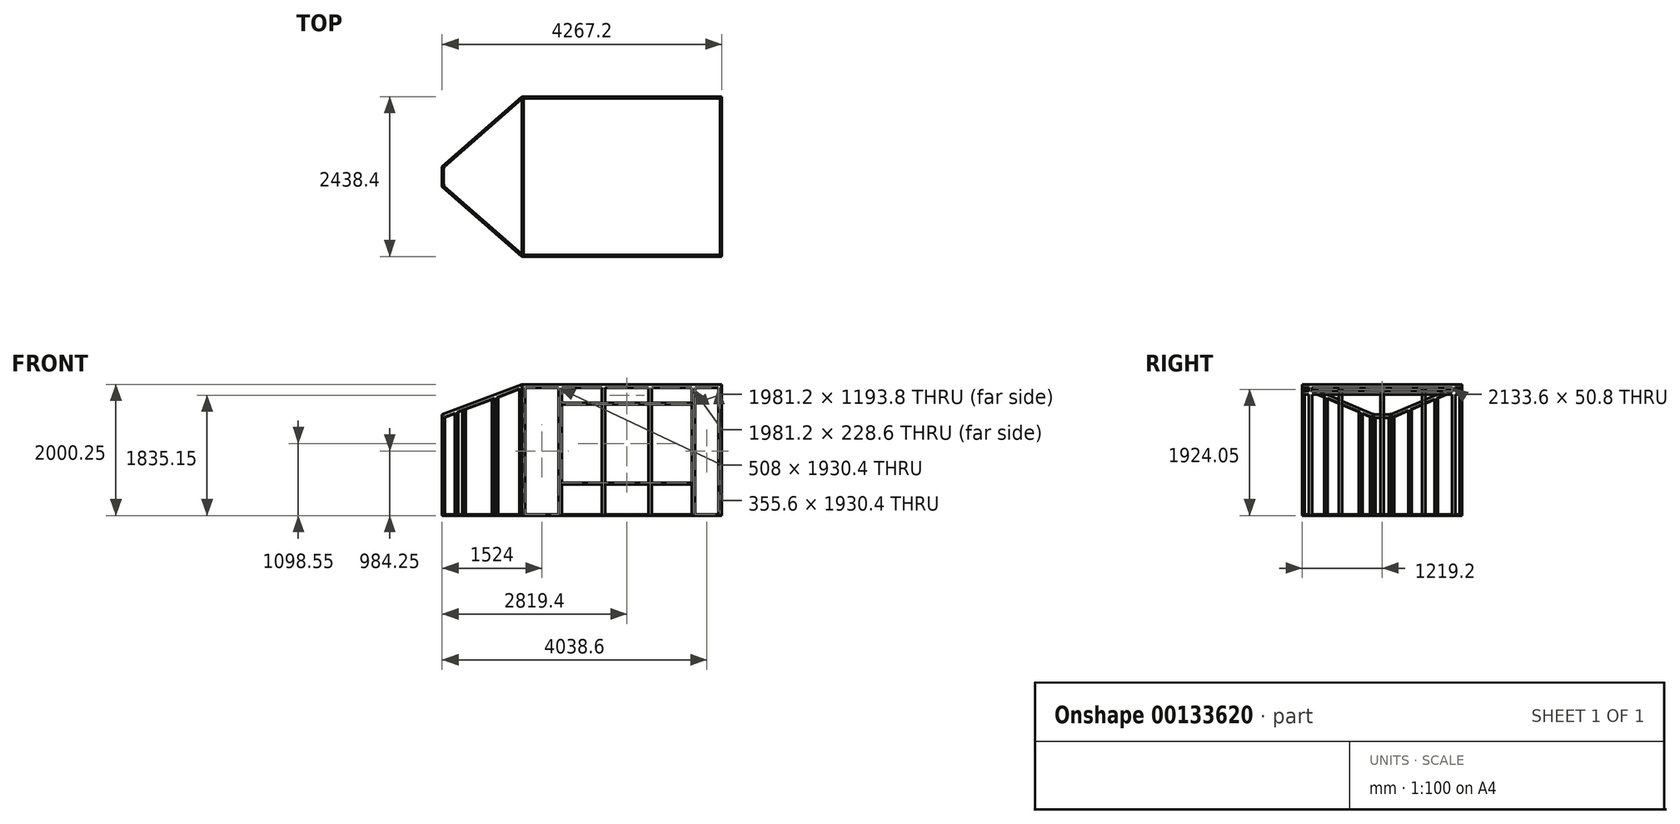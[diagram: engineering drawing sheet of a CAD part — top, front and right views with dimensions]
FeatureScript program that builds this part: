
annotation { "Feature Type Name" : "Feature", "Feature Type Description" : "" }
export const myFeature = defineFeature(function(context is Context, id is Id, definition is map)
    precondition{}
    {
        {
            var Q0;
            Q0=qCreatedBy(makeId("Top.planeOp"),FACE);
            var sketch = newSketch(context, id + "F0", { "sketchPlane" : qUnion([Q0])});
            skLineSegment(sketch, "E0.bottom", {"start": v(0, 0) * mm, "end": v(3048, 0) * mm});
            skLineSegment(sketch, "E0.top", {"start": v(0, 2438.4) * mm, "end": v(3048, 2438.4) * mm});
            skLineSegment(sketch, "E0.left", {"start": v(0, 0) * mm, "end": v(0, 2438.4) * mm});
            skLineSegment(sketch, "E0.right", {"start": v(3048, 0) * mm, "end": v(3048, 2438.4) * mm});
            skLineSegment(sketch, "E1", {"start": v(0, 1219.2) * mm, "end": v(-1219.2, 1219.2) * mm});
            skPoint(sketch, "E1.endSnap0", {"position": v(0, 1219.2) * mm});
            skLineSegment(sketch, "E2", {"start": v(-1219.2, 1219.2) * mm, "end": v(-1219.2, 1371.6) * mm});
            skLineSegment(sketch, "E3", {"start": v(-1219.2, 1371.6) * mm, "end": v(0, 2438.4) * mm});
            skLineSegment(sketch, "E4", {"start": v(-1219.2, 1219.2) * mm, "end": v(-1219.2, 1066.8) * mm});
            skLineSegment(sketch, "E5", {"start": v(-1219.2, 1066.8) * mm, "end": v(0, 0) * mm});
            skSolve(sketch);
        }
        {
            var Q0;
            {var subQ2=sQuery(id+"F0.wireOp",EDGE,"E1");Q0=makeQuery(id+"F0.imprint","IMPRINT",FACE,{"disambiguationData":[TD([[makeQuery(id+"F0.imprint","IMPRINT",EDGE,{"derivedFrom":subQ2}),-1.0]])]});}
            var Q1;
            {var subQ3=sQuery(id+"F0.wireOp",EDGE,"E0.bottom");Q1=makeQuery(id+"F0.imprint","IMPRINT",FACE,{"disambiguationData":[TD([[makeQuery(id+"F0.imprint","IMPRINT",EDGE,{"derivedFrom":subQ3}),1.0]])]});}
            var Q2;
            {var subQ2=sQuery(id+"F0.wireOp",EDGE,"E1");Q2=makeQuery(id+"F0.imprint","IMPRINT",FACE,{"disambiguationData":[TD([[makeQuery(id+"F0.imprint","IMPRINT",EDGE,{"derivedFrom":subQ2}),1.0]])]});}
            extrude(context, id + "F1", {"entities" : qUnion([Q0, Q1, Q2]), "depth" : 19.05 * mm});
        }
        {
            var Q0;
            Q0=makeQuery(id+"F1.opExtrude","CAP_FACE",FACE,{"disambiguationData":[OSD([sQuery(id+"F0.wireOp",EDGE,"E0.bottom"),sQuery(id+"F0.wireOp",EDGE,"E0.top"),sQuery(id+"F0.wireOp",EDGE,"E0.right"),sQuery(id+"F0.wireOp",EDGE,"E2"),sQuery(id+"F0.wireOp",EDGE,"E3"),sQuery(id+"F0.wireOp",EDGE,"E4"),sQuery(id+"F0.wireOp",EDGE,"E5")])],"isStart":false});
            var sketch = newSketch(context, id + "F2", { "sketchPlane" : qUnion([Q0])});
            skLineSegment(sketch, "E6.bottom", {"start": v(0, 2438.4) * mm, "end": v(50.8, 2438.4) * mm});
            skLineSegment(sketch, "E6.top", {"start": v(0, 2413) * mm, "end": v(50.8, 2413) * mm});
            skLineSegment(sketch, "E6.left", {"start": v(0, 2438.4) * mm, "end": v(0, 2413) * mm});
            skLineSegment(sketch, "E6.right", {"start": v(50.8, 2438.4) * mm, "end": v(50.8, 2413) * mm});
            skLineSegment(sketch, "E7.bottom", {"start": v(3048, 2438.4) * mm, "end": v(2997.2, 2438.4) * mm});
            skLineSegment(sketch, "E7.top", {"start": v(3048, 2413) * mm, "end": v(2997.2, 2413) * mm});
            skLineSegment(sketch, "E7.left", {"start": v(3048, 2438.4) * mm, "end": v(3048, 2413) * mm});
            skLineSegment(sketch, "E7.right", {"start": v(2997.2, 2438.4) * mm, "end": v(2997.2, 2413) * mm});
            skLineSegment(sketch, "E8.bottom", {"start": v(3048, 0) * mm, "end": v(2997.2, 0) * mm});
            skLineSegment(sketch, "E8.top", {"start": v(3048, 25.4) * mm, "end": v(2997.2, 25.4) * mm});
            skLineSegment(sketch, "E8.left", {"start": v(3048, 0) * mm, "end": v(3048, 25.4) * mm});
            skLineSegment(sketch, "E8.right", {"start": v(2997.2, 0) * mm, "end": v(2997.2, 25.4) * mm});
            skLineSegment(sketch, "E9.bottom", {"start": v(0, 0) * mm, "end": v(50.8, 0) * mm});
            skLineSegment(sketch, "E9.top", {"start": v(0, 25.4) * mm, "end": v(50.8, 25.4) * mm});
            skLineSegment(sketch, "E9.left", {"start": v(0, 0) * mm, "end": v(0, 25.4) * mm});
            skLineSegment(sketch, "E9.right", {"start": v(50.8, 0) * mm, "end": v(50.8, 25.4) * mm});
            skLineSegment(sketch, "E10.bottom", {"start": v(558.8, 2438.4) * mm, "end": v(609.6, 2438.4) * mm});
            skLineSegment(sketch, "E10.top", {"start": v(558.8, 2413) * mm, "end": v(609.6, 2413) * mm});
            skLineSegment(sketch, "E10.left", {"start": v(558.8, 2438.4) * mm, "end": v(558.8, 2413) * mm});
            skLineSegment(sketch, "E10.right", {"start": v(609.6, 2438.4) * mm, "end": v(609.6, 2413) * mm});
            skLineSegment(sketch, "E11.bottom", {"start": v(2641.6, 2438.4) * mm, "end": v(2590.8, 2438.4) * mm});
            skLineSegment(sketch, "E11.top", {"start": v(2641.6, 2413) * mm, "end": v(2590.8, 2413) * mm});
            skLineSegment(sketch, "E11.left", {"start": v(2641.6, 2438.4) * mm, "end": v(2641.6, 2413) * mm});
            skLineSegment(sketch, "E11.right", {"start": v(2590.8, 2438.4) * mm, "end": v(2590.8, 2413) * mm});
            skLineSegment(sketch, "E12.bottom", {"start": v(558.8, 0) * mm, "end": v(609.6, 0) * mm});
            skLineSegment(sketch, "E12.top", {"start": v(558.8, 25.4) * mm, "end": v(609.6, 25.4) * mm});
            skLineSegment(sketch, "E12.left", {"start": v(558.8, 0) * mm, "end": v(558.8, 25.4) * mm});
            skLineSegment(sketch, "E12.right", {"start": v(609.6, 0) * mm, "end": v(609.6, 25.4) * mm});
            skLineSegment(sketch, "E13.bottom", {"start": v(2641.6, 0) * mm, "end": v(2590.8, 0) * mm});
            skLineSegment(sketch, "E13.top", {"start": v(2641.6, 25.4) * mm, "end": v(2590.8, 25.4) * mm});
            skLineSegment(sketch, "E13.left", {"start": v(2641.6, 0) * mm, "end": v(2641.6, 25.4) * mm});
            skLineSegment(sketch, "E13.right", {"start": v(2590.8, 0) * mm, "end": v(2590.8, 25.4) * mm});
            skLineSegment(sketch, "E14.bottom", {"start": v(1981.2, 0) * mm, "end": v(1930.4, 0) * mm});
            skLineSegment(sketch, "E14.top", {"start": v(1981.2, 25.4) * mm, "end": v(1930.4, 25.4) * mm});
            skLineSegment(sketch, "E14.left", {"start": v(1981.2, 0) * mm, "end": v(1981.2, 25.4) * mm});
            skLineSegment(sketch, "E14.right", {"start": v(1930.4, 0) * mm, "end": v(1930.4, 25.4) * mm});
            skLineSegment(sketch, "E15.bottom", {"start": v(1270, 0) * mm, "end": v(1219.2, 0) * mm});
            skLineSegment(sketch, "E15.top", {"start": v(1270, 25.4) * mm, "end": v(1219.2, 25.4) * mm});
            skLineSegment(sketch, "E15.left", {"start": v(1270, 0) * mm, "end": v(1270, 25.4) * mm});
            skLineSegment(sketch, "E15.right", {"start": v(1219.2, 0) * mm, "end": v(1219.2, 25.4) * mm});
            skLineSegment(sketch, "E16.bottom", {"start": v(0, 1879.6) * mm, "end": v(25.4, 1879.6) * mm});
            skLineSegment(sketch, "E16.top", {"start": v(0, 1828.8) * mm, "end": v(25.4, 1828.8) * mm});
            skLineSegment(sketch, "E16.left", {"start": v(0, 1879.6) * mm, "end": v(0, 1828.8) * mm});
            skLineSegment(sketch, "E16.right", {"start": v(25.4, 1879.6) * mm, "end": v(25.4, 1828.8) * mm});
            skLineSegment(sketch, "E17.bottom", {"start": v(0, 558.8) * mm, "end": v(25.4, 558.8) * mm});
            skLineSegment(sketch, "E17.top", {"start": v(0, 609.6) * mm, "end": v(25.4, 609.6) * mm});
            skLineSegment(sketch, "E17.left", {"start": v(0, 558.8) * mm, "end": v(0, 609.6) * mm});
            skLineSegment(sketch, "E18", {"start": v(25.4, 609.6) * mm, "end": v(25.4, 558.8) * mm});
            skLineSegment(sketch, "E19", {"start": v(0, 1193.8) * mm, "end": v(0, 1244.6) * mm});
            skPoint(sketch, "E20.endSnap0", {"position": v(0, 1219.2) * mm});
            skLineSegment(sketch, "E21", {"start": v(25.4, 1219.2) * mm, "end": v(25.4, 1244.6) * mm});
            skLineSegment(sketch, "E22", {"start": v(25.4, 1244.6) * mm, "end": v(0, 1244.6) * mm});
            skLineSegment(sketch, "E23.MirrorCS", {"start": v(25.4, 1193.8) * mm, "end": v(0, 1193.8) * mm});
            skLineSegment(sketch, "E24.MirrorCS", {"start": v(25.4, 1219.2) * mm, "end": v(25.4, 1193.8) * mm});
            skSolve(sketch);
        }
        {
            var Q0;
            Q0=makeQuery(id+"F2.imprint","IMPRINT",FACE,{"disambiguationData":[TD([[makeQuery(id+"F2.imprint","IMPRINT",EDGE,{"derivedFrom":sQuery(id+"F2.wireOp",EDGE,"E6.bottom")}),-1.0]])]});
            var Q1;
            Q1=makeQuery(id+"F2.imprint","IMPRINT",FACE,{"disambiguationData":[TD([[makeQuery(id+"F2.imprint","IMPRINT",EDGE,{"derivedFrom":sQuery(id+"F2.wireOp",EDGE,"E10.bottom")}),-1.0]])]});
            var Q2;
            Q2=makeQuery(id+"F2.imprint","IMPRINT",FACE,{"disambiguationData":[TD([[makeQuery(id+"F2.imprint","IMPRINT",EDGE,{"derivedFrom":sQuery(id+"F2.wireOp",EDGE,"E11.bottom")}),-1.0]])]});
            var Q3;
            Q3=makeQuery(id+"F2.imprint","IMPRINT",FACE,{"disambiguationData":[TD([[makeQuery(id+"F2.imprint","IMPRINT",EDGE,{"derivedFrom":sQuery(id+"F2.wireOp",EDGE,"E7.bottom")}),-1.0]])]});
            var Q4;
            Q4=makeQuery(id+"F2.imprint","IMPRINT",FACE,{"disambiguationData":[TD([[makeQuery(id+"F2.imprint","IMPRINT",EDGE,{"derivedFrom":sQuery(id+"F2.wireOp",EDGE,"E8.bottom")}),1.0]])]});
            var Q5;
            Q5=makeQuery(id+"F2.imprint","IMPRINT",FACE,{"disambiguationData":[TD([[makeQuery(id+"F2.imprint","IMPRINT",EDGE,{"derivedFrom":sQuery(id+"F2.wireOp",EDGE,"E13.bottom")}),1.0]])]});
            var Q6;
            Q6=makeQuery(id+"F2.imprint","IMPRINT",FACE,{"disambiguationData":[TD([[makeQuery(id+"F2.imprint","IMPRINT",EDGE,{"derivedFrom":sQuery(id+"F2.wireOp",EDGE,"E14.bottom")}),1.0]])]});
            var Q7;
            Q7=makeQuery(id+"F2.imprint","IMPRINT",FACE,{"disambiguationData":[TD([[makeQuery(id+"F2.imprint","IMPRINT",EDGE,{"derivedFrom":sQuery(id+"F2.wireOp",EDGE,"E15.bottom")}),1.0]])]});
            var Q8;
            Q8=makeQuery(id+"F2.imprint","IMPRINT",FACE,{"disambiguationData":[TD([[makeQuery(id+"F2.imprint","IMPRINT",EDGE,{"derivedFrom":sQuery(id+"F2.wireOp",EDGE,"E12.bottom")}),1.0]])]});
            var Q9;
            Q9=makeQuery(id+"F2.imprint","IMPRINT",FACE,{"disambiguationData":[TD([[makeQuery(id+"F2.imprint","IMPRINT",EDGE,{"derivedFrom":sQuery(id+"F2.wireOp",EDGE,"E9.bottom")}),1.0]])]});
            var Q10;
            Q10=makeQuery(id+"F2.imprint","IMPRINT",FACE,{"disambiguationData":[TD([[makeQuery(id+"F2.imprint","IMPRINT",EDGE,{"derivedFrom":sQuery(id+"F2.wireOp",EDGE,"E17.bottom")}),1.0]])]});
            var Q11;
            Q11=makeQuery(id+"F2.imprint","IMPRINT",FACE,{"disambiguationData":[TD([[makeQuery(id+"F2.imprint","IMPRINT",EDGE,{"derivedFrom":sQuery(id+"F2.wireOp",EDGE,"E19")}),-1.0]])]});
            var Q12;
            Q12=makeQuery(id+"F2.imprint","IMPRINT",FACE,{"disambiguationData":[TD([[makeQuery(id+"F2.imprint","IMPRINT",EDGE,{"derivedFrom":sQuery(id+"F2.wireOp",EDGE,"E16.bottom")}),-1.0]])]});
            extrude(context, id + "F3", {"entities" : qUnion([Q0, Q1, Q2, Q3, Q4, Q5, Q6, Q7, Q8, Q9, Q10, Q11, Q12]), "operationType" : NewBodyOperationType.ADD, "depth" : 1981.2 * mm});
        }
        {
            var Q0;
            Q0=makeQuery(id+"F1.opExtrude","CAP_FACE",FACE,{"disambiguationData":[OSD([sQuery(id+"F0.wireOp",EDGE,"E0.bottom"),sQuery(id+"F0.wireOp",EDGE,"E0.top"),sQuery(id+"F0.wireOp",EDGE,"E0.right"),sQuery(id+"F0.wireOp",EDGE,"E2"),sQuery(id+"F0.wireOp",EDGE,"E3"),sQuery(id+"F0.wireOp",EDGE,"E4"),sQuery(id+"F0.wireOp",EDGE,"E5")])],"isStart":false});
            var sketch = newSketch(context, id + "F4", { "sketchPlane" : qUnion([Q0])});
            skLineSegment(sketch, "E25.bottom", {"start": v(1981.2, 2438.4) * mm, "end": v(1930.4, 2438.4) * mm});
            skLineSegment(sketch, "E25.top", {"start": v(1981.2, 2413) * mm, "end": v(1930.4, 2413) * mm});
            skLineSegment(sketch, "E25.left", {"start": v(1981.2, 2438.4) * mm, "end": v(1981.2, 2413) * mm});
            skLineSegment(sketch, "E25.right", {"start": v(1930.4, 2438.4) * mm, "end": v(1930.4, 2413) * mm});
            skLineSegment(sketch, "E26.bottom", {"start": v(1270, 2438.4) * mm, "end": v(1219.2, 2438.4) * mm});
            skLineSegment(sketch, "E26.top", {"start": v(1270, 2413) * mm, "end": v(1219.2, 2413) * mm});
            skLineSegment(sketch, "E26.left", {"start": v(1270, 2438.4) * mm, "end": v(1270, 2413) * mm});
            skLineSegment(sketch, "E26.right", {"start": v(1219.2, 2438.4) * mm, "end": v(1219.2, 2413) * mm});
            skPoint(sketch, "E27", {"position": v(609.6, 0) * mm});
            skPoint(sketch, "E28", {"position": v(1270, 0) * mm});
            skSolve(sketch);
        }
        {
            var Q0;
            Q0=makeQuery(id+"F4.imprint","IMPRINT",FACE,{"disambiguationData":[TD([[makeQuery(id+"F4.imprint","IMPRINT",EDGE,{"derivedFrom":sQuery(id+"F4.wireOp",EDGE,"E25.bottom")}),-1.0]])]});
            var Q1;
            Q1=makeQuery(id+"F4.imprint","IMPRINT",FACE,{"disambiguationData":[TD([[makeQuery(id+"F4.imprint","IMPRINT",EDGE,{"derivedFrom":sQuery(id+"F4.wireOp",EDGE,"E26.bottom")}),-1.0]])]});
            extrude(context, id + "F5", {"entities" : qUnion([Q0, Q1]), "operationType" : NewBodyOperationType.ADD, "depth" : 457.2 * mm});
        }
        {
            var Q0;
            Q0=makeQuery(id+"F3.opExtrude","SWEPT_FACE",FACE,{"disambiguationData":[OSD([sQuery(id+"F2.wireOp",EDGE,"E10.right")])]});
            var sketch = newSketch(context, id + "F6", { "sketchPlane" : qUnion([Q0])});
            skLineSegment(sketch, "E29.bottom", {"start": v(2438.4, 476.25) * mm, "end": v(2413, 476.25) * mm});
            skLineSegment(sketch, "E29.top", {"start": v(2438.4, 501.65) * mm, "end": v(2413, 501.65) * mm});
            skLineSegment(sketch, "E29.left", {"start": v(2438.4, 476.25) * mm, "end": v(2438.4, 501.65) * mm});
            skLineSegment(sketch, "E29.right", {"start": v(2413, 476.25) * mm, "end": v(2413, 501.65) * mm});
            skLineSegment(sketch, "E30.bottom", {"start": v(2438.4, 1695.45) * mm, "end": v(2413, 1695.45) * mm});
            skLineSegment(sketch, "E30.top", {"start": v(2438.4, 1720.85) * mm, "end": v(2413, 1720.85) * mm});
            skLineSegment(sketch, "E30.left", {"start": v(2438.4, 1695.45) * mm, "end": v(2438.4, 1720.85) * mm});
            skLineSegment(sketch, "E30.right", {"start": v(2413, 1695.45) * mm, "end": v(2413, 1720.85) * mm});
            skSolve(sketch);
        }
        {
            var Q0;
            Q0=makeQuery(id+"F6.imprint","IMPRINT",FACE,{"disambiguationData":[TD([[makeQuery(id+"F6.imprint","IMPRINT",EDGE,{"derivedFrom":sQuery(id+"F6.wireOp",EDGE,"E30.bottom")}),-1.0]])]});
            var Q1;
            Q1=makeQuery(id+"F6.imprint","IMPRINT",FACE,{"disambiguationData":[TD([[makeQuery(id+"F6.imprint","IMPRINT",EDGE,{"derivedFrom":sQuery(id+"F6.wireOp",EDGE,"E29.bottom")}),-1.0]])]});
            var Q2;
            Q2=makeQuery(id+"F3.opExtrude","SWEPT_FACE",FACE,{"disambiguationData":[OSD([sQuery(id+"F2.wireOp",EDGE,"E11.right")])]});
            extrude(context, id + "F7", {"entities" : qUnion([Q0, Q1]), "operationType" : NewBodyOperationType.ADD, "endBound" : BoundingType.UP_TO_SURFACE, "endBoundEntityFace" : qUnion([Q2]), "depth" : 25.4 * mm});
        }
        {
            var Q0;
            Q0=makeQuery(id+"F1.opExtrude","CAP_FACE",FACE,{"disambiguationData":[OSD([sQuery(id+"F0.wireOp",EDGE,"E0.bottom"),sQuery(id+"F0.wireOp",EDGE,"E0.top"),sQuery(id+"F0.wireOp",EDGE,"E0.right"),sQuery(id+"F0.wireOp",EDGE,"E2"),sQuery(id+"F0.wireOp",EDGE,"E3"),sQuery(id+"F0.wireOp",EDGE,"E4"),sQuery(id+"F0.wireOp",EDGE,"E5")])],"isStart":false});
            var sketch = newSketch(context, id + "F8", { "sketchPlane" : qUnion([Q0])});
            skLineSegment(sketch, "E31.bottom", {"start": v(3048, 101.6) * mm, "end": v(3022.6, 101.6) * mm});
            skLineSegment(sketch, "E31.top", {"start": v(3048, 152.4) * mm, "end": v(3022.6, 152.4) * mm});
            skLineSegment(sketch, "E31.left", {"start": v(3048, 101.6) * mm, "end": v(3048, 152.4) * mm});
            skLineSegment(sketch, "E31.right", {"start": v(3022.6, 101.6) * mm, "end": v(3022.6, 152.4) * mm});
            skLineSegment(sketch, "E32.bottom", {"start": v(3048, 2336.8) * mm, "end": v(3022.6, 2336.8) * mm});
            skLineSegment(sketch, "E32.top", {"start": v(3048, 2286) * mm, "end": v(3022.6, 2286) * mm});
            skLineSegment(sketch, "E32.left", {"start": v(3048, 2336.8) * mm, "end": v(3048, 2286) * mm});
            skLineSegment(sketch, "E32.right", {"start": v(3022.6, 2336.8) * mm, "end": v(3022.6, 2286) * mm});
            skSolve(sketch);
        }
        {
            var Q0;
            Q0=makeQuery(id+"F8.imprint","IMPRINT",FACE,{"disambiguationData":[TD([[makeQuery(id+"F8.imprint","IMPRINT",EDGE,{"derivedFrom":sQuery(id+"F8.wireOp",EDGE,"E32.bottom")}),1.0]])]});
            var Q1;
            Q1=makeQuery(id+"F8.imprint","IMPRINT",FACE,{"disambiguationData":[TD([[makeQuery(id+"F8.imprint","IMPRINT",EDGE,{"derivedFrom":sQuery(id+"F8.wireOp",EDGE,"E31.bottom")}),-1.0]])]});
            extrude(context, id + "F9", {"entities" : qUnion([Q0, Q1]), "operationType" : NewBodyOperationType.ADD, "depth" : 1981.2 * mm});
        }
        {
            var Q0;
            Q0=makeQuery(id+"F9.boolean.opBoolean","MERGE",FACE,{"derivedFrom":[makeQuery(id+"F3.boolean.opBoolean","MERGE",FACE,{"derivedFrom":[makeQuery(id+"F1.opExtrude","SWEPT_FACE",FACE,{"disambiguationData":[OSD([sQuery(id+"F0.wireOp",EDGE,"E0.right")])]}),makeQuery(id+"F3.opExtrude","SWEPT_FACE",FACE,{"disambiguationData":[OSD([sQuery(id+"F2.wireOp",EDGE,"E7.left")])]}),makeQuery(id+"F3.opExtrude","SWEPT_FACE",FACE,{"disambiguationData":[OSD([sQuery(id+"F2.wireOp",EDGE,"E8.left")])]})]}),makeQuery(id+"F9.opExtrude","SWEPT_FACE",FACE,{"disambiguationData":[OSD([sQuery(id+"F8.wireOp",EDGE,"E31.left")])]}),makeQuery(id+"F9.opExtrude","SWEPT_FACE",FACE,{"disambiguationData":[OSD([sQuery(id+"F8.wireOp",EDGE,"E32.left")])]})]});
            var sketch = newSketch(context, id + "F10", { "sketchPlane" : qUnion([Q0])});
            skLineSegment(sketch, "E33.bottom", {"start": v(2413, 2000.25) * mm, "end": v(2438.4, 2000.25) * mm});
            skLineSegment(sketch, "E33.top", {"start": v(2413, 1949.45) * mm, "end": v(2438.4, 1949.45) * mm});
            skLineSegment(sketch, "E33.left", {"start": v(2413, 2000.25) * mm, "end": v(2413, 1949.45) * mm});
            skLineSegment(sketch, "E33.right", {"start": v(2438.4, 2000.25) * mm, "end": v(2438.4, 1949.45) * mm});
            skSolve(sketch);
        }
        {
            var Q0;
            Q0=makeQuery(id+"F10.imprint","IMPRINT",FACE,{"disambiguationData":[TD([[makeQuery(id+"F10.imprint","IMPRINT",EDGE,{"derivedFrom":sQuery(id+"F10.wireOp",EDGE,"E33.bottom")}),-1.0]])]});
            var Q1;
            Q1=makeQuery(id+"F3.opExtrude","SWEPT_FACE",FACE,{"disambiguationData":[OSD([sQuery(id+"F2.wireOp",EDGE,"E6.right")])]});
            extrude(context, id + "F11", {"entities" : qUnion([Q0]), "operationType" : NewBodyOperationType.ADD, "endBound" : BoundingType.UP_TO_SURFACE, "oppositeDirection" : true, "endBoundEntityFace" : qUnion([Q1]), "depth" : 25.4 * mm});
        }
        {
            var Q0;
            Q0=makeQuery(id+"F9.boolean.opBoolean","MERGE",FACE,{"derivedFrom":[makeQuery(id+"F3.boolean.opBoolean","MERGE",FACE,{"derivedFrom":[makeQuery(id+"F1.opExtrude","SWEPT_FACE",FACE,{"disambiguationData":[OSD([sQuery(id+"F0.wireOp",EDGE,"E0.right")])]}),makeQuery(id+"F3.opExtrude","SWEPT_FACE",FACE,{"disambiguationData":[OSD([sQuery(id+"F2.wireOp",EDGE,"E7.left")])]}),makeQuery(id+"F3.opExtrude","SWEPT_FACE",FACE,{"disambiguationData":[OSD([sQuery(id+"F2.wireOp",EDGE,"E8.left")])]})]}),makeQuery(id+"F9.opExtrude","SWEPT_FACE",FACE,{"disambiguationData":[OSD([sQuery(id+"F8.wireOp",EDGE,"E31.left")])]}),makeQuery(id+"F9.opExtrude","SWEPT_FACE",FACE,{"disambiguationData":[OSD([sQuery(id+"F8.wireOp",EDGE,"E32.left")])]})]});
            var sketch = newSketch(context, id + "F12", { "sketchPlane" : qUnion([Q0])});
            skLineSegment(sketch, "E34.bottom", {"start": v(0, 2000.25) * mm, "end": v(25.4, 2000.25) * mm});
            skLineSegment(sketch, "E34.top", {"start": v(0, 1949.45) * mm, "end": v(25.4, 1949.45) * mm});
            skLineSegment(sketch, "E34.left", {"start": v(0, 2000.25) * mm, "end": v(0, 1949.45) * mm});
            skLineSegment(sketch, "E34.right", {"start": v(25.4, 2000.25) * mm, "end": v(25.4, 1949.45) * mm});
            skSolve(sketch);
        }
        {
            var Q0;
            Q0=makeQuery(id+"F12.imprint","IMPRINT",FACE,{"disambiguationData":[TD([[makeQuery(id+"F12.imprint","IMPRINT",EDGE,{"derivedFrom":sQuery(id+"F12.wireOp",EDGE,"E34.bottom")}),-1.0]])]});
            var Q1;
            Q1=makeQuery(id+"F3.opExtrude","SWEPT_FACE",FACE,{"disambiguationData":[OSD([sQuery(id+"F2.wireOp",EDGE,"E9.right")])]});
            extrude(context, id + "F13", {"entities" : qUnion([Q0]), "operationType" : NewBodyOperationType.ADD, "endBound" : BoundingType.UP_TO_SURFACE, "oppositeDirection" : true, "endBoundEntityFace" : qUnion([Q1]), "depth" : 25.4 * mm});
        }
        {
            var Q0;
            Q0=makeQuery(id+"F13.boolean.opBoolean","MERGE",FACE,{"derivedFrom":[makeQuery(id+"F3.boolean.opBoolean","MERGE",FACE,{"derivedFrom":[makeQuery(id+"F1.opExtrude","SWEPT_FACE",FACE,{"disambiguationData":[OSD([sQuery(id+"F0.wireOp",EDGE,"E0.bottom")])]}),makeQuery(id+"F3.opExtrude","SWEPT_FACE",FACE,{"disambiguationData":[OSD([sQuery(id+"F2.wireOp",EDGE,"E8.bottom")])]}),makeQuery(id+"F3.opExtrude","SWEPT_FACE",FACE,{"disambiguationData":[OSD([sQuery(id+"F2.wireOp",EDGE,"E9.bottom")])]}),makeQuery(id+"F3.opExtrude","SWEPT_FACE",FACE,{"disambiguationData":[OSD([sQuery(id+"F2.wireOp",EDGE,"E12.bottom")])]}),makeQuery(id+"F3.opExtrude","SWEPT_FACE",FACE,{"disambiguationData":[OSD([sQuery(id+"F2.wireOp",EDGE,"E13.bottom")])]}),makeQuery(id+"F3.opExtrude","SWEPT_FACE",FACE,{"disambiguationData":[OSD([sQuery(id+"F2.wireOp",EDGE,"E14.bottom")])]}),makeQuery(id+"F3.opExtrude","SWEPT_FACE",FACE,{"disambiguationData":[OSD([sQuery(id+"F2.wireOp",EDGE,"E15.bottom")])]})]}),makeQuery(id+"F13.opExtrude","SWEPT_FACE",FACE,{"disambiguationData":[OSD([sQuery(id+"F12.wireOp",EDGE,"E34.left")])]})]});
            var sketch = newSketch(context, id + "F14", { "sketchPlane" : qUnion([Q0])});
            skLineSegment(sketch, "E35.bottom", {"start": v(0, 2000.25) * mm, "end": v(25.4, 2000.25) * mm});
            skLineSegment(sketch, "E35.top", {"start": v(0, 1949.45) * mm, "end": v(25.4, 1949.45) * mm});
            skLineSegment(sketch, "E35.left", {"start": v(0, 2000.25) * mm, "end": v(0, 1949.45) * mm});
            skLineSegment(sketch, "E35.right", {"start": v(25.4, 2000.25) * mm, "end": v(25.4, 1949.45) * mm});
            skLineSegment(sketch, "E36.bottom", {"start": v(3048, 2000.25) * mm, "end": v(3022.6, 2000.25) * mm});
            skLineSegment(sketch, "E36.top", {"start": v(3048, 1949.45) * mm, "end": v(3022.6, 1949.45) * mm});
            skLineSegment(sketch, "E36.left", {"start": v(3048, 2000.25) * mm, "end": v(3048, 1949.45) * mm});
            skLineSegment(sketch, "E36.right", {"start": v(3022.6, 2000.25) * mm, "end": v(3022.6, 1949.45) * mm});
            skSolve(sketch);
        }
        {
            var Q0;
            Q0=makeQuery(id+"F14.imprint","IMPRINT",FACE,{"disambiguationData":[TD([[makeQuery(id+"F14.imprint","IMPRINT",EDGE,{"derivedFrom":sQuery(id+"F14.wireOp",EDGE,"E36.bottom")}),-1.0]])]});
            var Q1;
            Q1=makeQuery(id+"F14.imprint","IMPRINT",FACE,{"disambiguationData":[TD([[makeQuery(id+"F14.imprint","IMPRINT",EDGE,{"derivedFrom":sQuery(id+"F14.wireOp",EDGE,"E35.bottom")}),-1.0]])]});
            var Q2;
            Q2=makeQuery(id+"F11.boolean.opBoolean","MERGE",FACE,{"derivedFrom":[makeQuery(id+"F3.opExtrude","SWEPT_FACE",FACE,{"disambiguationData":[OSD([sQuery(id+"F2.wireOp",EDGE,"E6.top")])]}),makeQuery(id+"F3.opExtrude","SWEPT_FACE",FACE,{"disambiguationData":[OSD([sQuery(id+"F2.wireOp",EDGE,"E7.top")])]}),makeQuery(id+"F7.boolean.opBoolean","MERGE",FACE,{"derivedFrom":[makeQuery(id+"F3.opExtrude","SWEPT_FACE",FACE,{"disambiguationData":[OSD([sQuery(id+"F2.wireOp",EDGE,"E10.top")])]}),makeQuery(id+"F3.opExtrude","SWEPT_FACE",FACE,{"disambiguationData":[OSD([sQuery(id+"F2.wireOp",EDGE,"E11.top")])]}),makeQuery(id+"F5.opExtrude","SWEPT_FACE",FACE,{"disambiguationData":[OSD([sQuery(id+"F4.wireOp",EDGE,"E25.top")])]}),makeQuery(id+"F5.opExtrude","SWEPT_FACE",FACE,{"disambiguationData":[OSD([sQuery(id+"F4.wireOp",EDGE,"E26.top")])]}),makeQuery(id+"F7.opExtrude","SWEPT_FACE",FACE,{"disambiguationData":[OSD([sQuery(id+"F6.wireOp",EDGE,"E29.right")])]}),makeQuery(id+"F7.opExtrude","SWEPT_FACE",FACE,{"disambiguationData":[OSD([sQuery(id+"F6.wireOp",EDGE,"E30.right")])]})]}),makeQuery(id+"F11.opExtrude","SWEPT_FACE",FACE,{"disambiguationData":[OSD([sQuery(id+"F10.wireOp",EDGE,"E33.left")])]})]});
            extrude(context, id + "F15", {"entities" : qUnion([Q0, Q1]), "operationType" : NewBodyOperationType.ADD, "endBound" : BoundingType.UP_TO_SURFACE, "oppositeDirection" : true, "endBoundEntityFace" : qUnion([Q2]), "depth" : 25.4 * mm});
        }
        {
            var Q0;
            Q0=makeQuery(id+"F1.opExtrude","CAP_FACE",FACE,{"disambiguationData":[OSD([sQuery(id+"F0.wireOp",EDGE,"E0.bottom"),sQuery(id+"F0.wireOp",EDGE,"E0.top"),sQuery(id+"F0.wireOp",EDGE,"E0.right"),sQuery(id+"F0.wireOp",EDGE,"E2"),sQuery(id+"F0.wireOp",EDGE,"E3"),sQuery(id+"F0.wireOp",EDGE,"E4"),sQuery(id+"F0.wireOp",EDGE,"E5")])],"isStart":false});
            var sketch = newSketch(context, id + "F16", { "sketchPlane" : qUnion([Q0])});
            skLineSegment(sketch, "E37", {"start": v(-1219.2, 1371.6) * mm, "end": v(-1180.97, 1405.05) * mm});
            skLineSegment(sketch, "E38", {"start": v(-1219.2, 1371.6) * mm, "end": v(-1219.2, 1320.8) * mm});
            skLineSegment(sketch, "E39", {"start": v(-1219.2, 1066.8) * mm, "end": v(-1219.2, 1117.6) * mm});
            skLineSegment(sketch, "E40", {"start": v(-1219.2, 1066.8) * mm, "end": v(-1180.97, 1033.35) * mm});
            skLineSegment(sketch, "E41", {"start": v(0, 2438.4) * mm, "end": v(-38.23, 2404.95) * mm});
            skLineSegment(sketch, "E42", {"start": v(0, 0) * mm, "end": v(-38.23, 33.45) * mm});
            skLineSegment(sketch, "E43.0", {"start": v(-1212.85, 1368.72) * mm, "end": v(-1176.79, 1400.27) * mm});
            skLineSegment(sketch, "E43.1", {"start": v(-1212.85, 1368.72) * mm, "end": v(-1212.85, 1320.8) * mm});
            skLineSegment(sketch, "E44.0", {"start": v(-1212.85, 1069.68) * mm, "end": v(-1212.85, 1117.6) * mm});
            skLineSegment(sketch, "E44.1", {"start": v(-1212.85, 1069.68) * mm, "end": v(-1176.79, 1038.13) * mm});
            skLineSegment(sketch, "E45.0", {"start": v(0, 8.44) * mm, "end": v(-34.05, 38.23) * mm});
            skLineSegment(sketch, "E46.0", {"start": v(0, 2429.96) * mm, "end": v(-34.05, 2400.17) * mm});
            skLineSegment(sketch, "E47", {"start": v(-38.23, 2404.95) * mm, "end": v(-34.05, 2400.17) * mm});
            skLineSegment(sketch, "E48", {"start": v(0, 2438.4) * mm, "end": v(0, 2429.96) * mm});
            skLineSegment(sketch, "E49", {"start": v(-38.23, 33.45) * mm, "end": v(-34.05, 38.23) * mm});
            skLineSegment(sketch, "E50", {"start": v(0, 0) * mm, "end": v(0, 8.44) * mm});
            skLineSegment(sketch, "E51", {"start": v(-1212.85, 1117.6) * mm, "end": v(-1219.2, 1117.6) * mm});
            skLineSegment(sketch, "E52", {"start": v(-1176.79, 1038.13) * mm, "end": v(-1180.97, 1033.35) * mm});
            skLineSegment(sketch, "E53", {"start": v(-1212.85, 1320.8) * mm, "end": v(-1219.2, 1320.8) * mm});
            skLineSegment(sketch, "E54", {"start": v(-1176.79, 1400.27) * mm, "end": v(-1180.97, 1405.05) * mm});
            skLineSegment(sketch, "E55.bottom", {"start": v(-1212.85, 1368.72) * mm, "end": v(-1187.45, 1368.72) * mm});
            skLineSegment(sketch, "E55.top", {"start": v(-1212.85, 1343.32) * mm, "end": v(-1187.45, 1343.32) * mm});
            skLineSegment(sketch, "E55.left", {"start": v(-1212.85, 1368.72) * mm, "end": v(-1212.85, 1343.32) * mm});
            skLineSegment(sketch, "E55.right", {"start": v(-1187.45, 1368.72) * mm, "end": v(-1187.45, 1343.32) * mm});
            skLineSegment(sketch, "E56.bottom", {"start": v(-1212.85, 1069.68) * mm, "end": v(-1187.45, 1069.68) * mm});
            skLineSegment(sketch, "E56.top", {"start": v(-1212.85, 1095.08) * mm, "end": v(-1187.45, 1095.08) * mm});
            skLineSegment(sketch, "E56.left", {"start": v(-1212.85, 1069.68) * mm, "end": v(-1212.85, 1095.08) * mm});
            skLineSegment(sketch, "E56.right", {"start": v(-1187.45, 1069.68) * mm, "end": v(-1187.45, 1095.08) * mm});
            skLineSegment(sketch, "E57", {"start": v(-913.35, 1639.22) * mm, "end": v(-875.12, 1672.67) * mm});
            skLineSegment(sketch, "E58", {"start": v(-875.12, 1672.67) * mm, "end": v(-858.4, 1653.55) * mm});
            skLineSegment(sketch, "E59", {"start": v(-858.4, 1653.55) * mm, "end": v(-896.63, 1620.1) * mm});
            skLineSegment(sketch, "E60", {"start": v(-913.35, 1639.22) * mm, "end": v(-896.63, 1620.1) * mm});
            skLineSegment(sketch, "E61", {"start": v(-382.3, 334.52) * mm, "end": v(-420.54, 367.97) * mm});
            skLineSegment(sketch, "E62", {"start": v(-420.54, 367.97) * mm, "end": v(-403.81, 387.09) * mm});
            skLineSegment(sketch, "E63", {"start": v(-403.81, 387.09) * mm, "end": v(-365.58, 353.64) * mm});
            skLineSegment(sketch, "E64", {"start": v(-382.3, 334.52) * mm, "end": v(-365.58, 353.64) * mm});
            skLineSegment(sketch, "E65", {"start": v(-989.81, 866.09) * mm, "end": v(-1028.05, 899.54) * mm});
            skLineSegment(sketch, "E66", {"start": v(-1028.05, 899.54) * mm, "end": v(-1011.32, 918.66) * mm});
            skLineSegment(sketch, "E67", {"start": v(-1011.32, 918.66) * mm, "end": v(-973.09, 885.2) * mm});
            skLineSegment(sketch, "E68", {"start": v(-989.81, 866.09) * mm, "end": v(-973.09, 885.2) * mm});
            skLineSegment(sketch, "E69", {"start": v(-420.54, 2070.43) * mm, "end": v(-458.77, 2036.98) * mm});
            skLineSegment(sketch, "E70", {"start": v(-458.77, 2036.98) * mm, "end": v(-442.04, 2017.86) * mm});
            skLineSegment(sketch, "E71", {"start": v(-442.04, 2017.86) * mm, "end": v(-403.81, 2051.31) * mm});
            skLineSegment(sketch, "E72", {"start": v(-420.54, 2070.43) * mm, "end": v(-403.81, 2051.31) * mm});
            skSolve(sketch);
        }
        {
            var Q0;
            Q0=makeQuery(id+"F16.imprint","IMPRINT",FACE,{"disambiguationData":[TD([[makeQuery(id+"F16.imprint","IMPRINT",EDGE,{"derivedFrom":sQuery(id+"F16.wireOp",EDGE,"E61")}),1.0]])]});
            var Q1;
            Q1=makeQuery(id+"F16.imprint","IMPRINT",FACE,{"disambiguationData":[TD([[makeQuery(id+"F16.imprint","IMPRINT",EDGE,{"derivedFrom":sQuery(id+"F16.wireOp",EDGE,"E42")}),1.0]])]});
            var Q2;
            Q2=makeQuery(id+"F16.imprint","IMPRINT",FACE,{"disambiguationData":[TD([[makeQuery(id+"F16.imprint","IMPRINT",EDGE,{"derivedFrom":sQuery(id+"F16.wireOp",EDGE,"E65")}),1.0]])]});
            var Q3;
            Q3=makeQuery(id+"F16.imprint","IMPRINT",FACE,{"disambiguationData":[TD([[makeQuery(id+"F16.imprint","IMPRINT",EDGE,{"derivedFrom":sQuery(id+"F16.wireOp",EDGE,"E56.bottom")}),1.0]])]});
            var Q4;
            Q4=makeQuery(id+"F16.imprint","IMPRINT",FACE,{"disambiguationData":[TD([[makeQuery(id+"F16.imprint","IMPRINT",EDGE,{"derivedFrom":sQuery(id+"F16.wireOp",EDGE,"E39")}),-1.0]])]});
            var Q5;
            Q5=makeQuery(id+"F16.imprint","IMPRINT",FACE,{"disambiguationData":[TD([[makeQuery(id+"F16.imprint","IMPRINT",EDGE,{"derivedFrom":sQuery(id+"F16.wireOp",EDGE,"E55.bottom")}),-1.0]])]});
            var Q6;
            Q6=makeQuery(id+"F16.imprint","IMPRINT",FACE,{"disambiguationData":[TD([[makeQuery(id+"F16.imprint","IMPRINT",EDGE,{"derivedFrom":sQuery(id+"F16.wireOp",EDGE,"E37")}),-1.0]])]});
            var Q7;
            Q7=makeQuery(id+"F16.imprint","IMPRINT",FACE,{"disambiguationData":[TD([[makeQuery(id+"F16.imprint","IMPRINT",EDGE,{"derivedFrom":sQuery(id+"F16.wireOp",EDGE,"E57")}),-1.0]])]});
            var Q8;
            Q8=makeQuery(id+"F16.imprint","IMPRINT",FACE,{"disambiguationData":[TD([[makeQuery(id+"F16.imprint","IMPRINT",EDGE,{"derivedFrom":sQuery(id+"F16.wireOp",EDGE,"E69")}),-1.0]])]});
            var Q9;
            Q9=makeQuery(id+"F16.imprint","IMPRINT",FACE,{"disambiguationData":[TD([[makeQuery(id+"F16.imprint","IMPRINT",EDGE,{"derivedFrom":sQuery(id+"F16.wireOp",EDGE,"E41")}),-1.0]])]});
            extrude(context, id + "F17", {"entities" : qUnion([Q0, Q1, Q2, Q3, Q4, Q5, Q6, Q7, Q8, Q9]), "operationType" : NewBodyOperationType.ADD, "depth" : 1981.2 * mm});
        }
        {
            var Q0;
            Q0=makeQuery(id+"F17.boolean.opBoolean","MERGE",FACE,{"derivedFrom":[makeQuery(id+"F1.opExtrude","SWEPT_FACE",FACE,{"disambiguationData":[OSD([sQuery(id+"F0.wireOp",EDGE,"E5")])]}),makeQuery(id+"F17.opExtrude","SWEPT_FACE",FACE,{"disambiguationData":[OSD([sQuery(id+"F16.wireOp",EDGE,"E40")])]}),makeQuery(id+"F17.opExtrude","SWEPT_FACE",FACE,{"disambiguationData":[OSD([sQuery(id+"F16.wireOp",EDGE,"E42")])]}),makeQuery(id+"F17.opExtrude","SWEPT_FACE",FACE,{"disambiguationData":[OSD([sQuery(id+"F16.wireOp",EDGE,"E61")])]}),makeQuery(id+"F17.opExtrude","SWEPT_FACE",FACE,{"disambiguationData":[OSD([sQuery(id+"F16.wireOp",EDGE,"E65")])]})]});
            var sketch = newSketch(context, id + "F18", { "sketchPlane" : qUnion([Q0])});
            skLineSegment(sketch, "E73", {"start": v(0, 2000.25) * mm, "end": v(-1620.03, 1543.05) * mm});
            skLineSegment(sketch, "E74", {"start": v(-1620.03, 1543.05) * mm, "end": v(-1620.03, 2000.25) * mm});
            skLineSegment(sketch, "E75", {"start": v(-1620.03, 2000.25) * mm, "end": v(0, 2000.25) * mm});
            skSolve(sketch);
        }
        {
            var Q0;
            {var subQ0=sQuery(id+"F18.wireOp",EDGE,"E74");Q0=makeQuery(id+"F18.imprint","IMPRINT",FACE,{"disambiguationData":[TD([[makeQuery(id+"F18.imprint","IMPRINT",EDGE,{"derivedFrom":subQ0}),1.0]])]});}
            var Q1;
            {var subQ0=sQuery(id+"F18.wireOp",EDGE,"E73");var subQ1=sQuery(id+"F16.wireOp",EDGE,"E65");var subQ2=sQuery(id+"F0.wireOp",EDGE,"E5");var subQ3=makeQuery(id+"F17.opExtrude","SWEPT_EDGE",EDGE,{"disambiguationData":[OSD([subQ2,subQ1,sQuery(id+"F16.wireOp",EDGE,"E68")])]});var subQ4=makeQuery(id+"F18.imprint","INTERSECT",VERTEX,{"derivedFrom":[subQ3,subQ0]});Q1=makeQuery(id+"F18.imprint","IMPRINT",FACE,{"disambiguationData":[TD([[makeQuery(id+"F18.imprint","IMPRINT",EDGE,{"disambiguationData":[TD([[subQ4,-1.0]])],"derivedFrom":subQ0}),-1.0]])]});}
            var Q2;
            {var subQ0=sQuery(id+"F18.wireOp",EDGE,"E73");var subQ1=sQuery(id+"F16.wireOp",EDGE,"E61");var subQ2=sQuery(id+"F0.wireOp",EDGE,"E5");var subQ3=makeQuery(id+"F17.opExtrude","SWEPT_EDGE",EDGE,{"disambiguationData":[OSD([subQ2,subQ1,sQuery(id+"F16.wireOp",EDGE,"E64")])]});var subQ4=makeQuery(id+"F18.imprint","INTERSECT",VERTEX,{"derivedFrom":[subQ3,subQ0]});Q2=makeQuery(id+"F18.imprint","IMPRINT",FACE,{"disambiguationData":[TD([[makeQuery(id+"F18.imprint","IMPRINT",EDGE,{"disambiguationData":[TD([[subQ4,-1.0]])],"derivedFrom":subQ0}),-1.0]])]});}
            var Q3;
            {var subQ0=sQuery(id+"F18.wireOp",EDGE,"E75");var subQ2=sQuery(id+"F16.wireOp",EDGE,"E42");var subQ3=sQuery(id+"F0.wireOp",EDGE,"E5");var subQ5=makeQuery(id+"F17.opExtrude","SWEPT_EDGE",EDGE,{"disambiguationData":[OSD([subQ3,subQ2,sQuery(id+"F16.wireOp",EDGE,"E49")])]});var subQ7=makeQuery(id+"F18.imprint","INTERSECT",VERTEX,{"derivedFrom":[subQ5,subQ0]});Q3=makeQuery(id+"F18.imprint","IMPRINT",FACE,{"disambiguationData":[TD([[makeQuery(id+"F18.imprint","IMPRINT",EDGE,{"disambiguationData":[TD([[subQ7,-1.0]])],"derivedFrom":subQ5}),1.0]])]});}
            var Q4;
            Q4=makeQuery(id+"F17.opExtrude","SWEPT_FACE",FACE,{"disambiguationData":[OSD([sQuery(id+"F16.wireOp",EDGE,"E51")])]});
            extrude(context, id + "F19", {"entities" : qUnion([Q0, Q1, Q2, Q3]), "operationType" : NewBodyOperationType.REMOVE, "endBound" : BoundingType.UP_TO_SURFACE, "oppositeDirection" : true, "endBoundEntityFace" : qUnion([Q4]), "depth" : 25.4 * mm});
        }
        {
            var Q0;
            Q0=makeQuery(id+"F19.boolean.opBoolean","COPY",FACE,{"derivedFrom":makeQuery(id+"F19.opExtrude","SWEPT_FACE",FACE,{"disambiguationData":[OSD([sQuery(id+"F18.wireOp",EDGE,"E74")])]})});
            extrude(context, id + "F20", {"entities" : qUnion([Q0]), "operationType" : NewBodyOperationType.REMOVE, "endBound" : BoundingType.THROUGH_ALL, "oppositeDirection" : true, "depth" : 25.4 * mm});
        }
        {
            var Q0;
            Q0=makeQuery(id+"F17.opExtrude","CAP_FACE",FACE,{"disambiguationData":[OSD([sQuery(id+"F16.wireOp",EDGE,"E39"),sQuery(id+"F16.wireOp",EDGE,"E40"),sQuery(id+"F16.wireOp",EDGE,"E44.0"),sQuery(id+"F16.wireOp",EDGE,"E44.1"),sQuery(id+"F16.wireOp",EDGE,"E51"),sQuery(id+"F16.wireOp",EDGE,"E52"),sQuery(id+"F16.wireOp",EDGE,"E56.bottom"),sQuery(id+"F16.wireOp",EDGE,"E56.top"),sQuery(id+"F16.wireOp",EDGE,"E56.right")])],"isStart":false});
            extrude(context, id + "F21", {"entities" : qUnion([Q0]), "operationType" : NewBodyOperationType.REMOVE, "oppositeDirection" : true, "depth" : 457.2 * mm});
        }
        {
            var Q0;
            Q0=makeQuery(id+"F17.boolean.opBoolean","MERGE",FACE,{"derivedFrom":[makeQuery(id+"F1.opExtrude","SWEPT_FACE",FACE,{"disambiguationData":[OSD([sQuery(id+"F0.wireOp",EDGE,"E3")])]}),makeQuery(id+"F17.opExtrude","SWEPT_FACE",FACE,{"disambiguationData":[OSD([sQuery(id+"F16.wireOp",EDGE,"E37")])]}),makeQuery(id+"F17.opExtrude","SWEPT_FACE",FACE,{"disambiguationData":[OSD([sQuery(id+"F16.wireOp",EDGE,"E41")])]}),makeQuery(id+"F17.opExtrude","SWEPT_FACE",FACE,{"disambiguationData":[OSD([sQuery(id+"F16.wireOp",EDGE,"E57")])]}),makeQuery(id+"F17.opExtrude","SWEPT_FACE",FACE,{"disambiguationData":[OSD([sQuery(id+"F16.wireOp",EDGE,"E69")])]})]});
            var sketch = newSketch(context, id + "F22", { "sketchPlane" : qUnion([Q0])});
            skLineSegment(sketch, "E76", {"start": v(-1605.7, 2000.25) * mm, "end": v(14.34, 1543.05) * mm});
            skLineSegment(sketch, "E77", {"start": v(14.34, 1543.05) * mm, "end": v(14.34, 2000.25) * mm});
            skLineSegment(sketch, "E78", {"start": v(14.34, 2000.25) * mm, "end": v(-1605.7, 2000.25) * mm});
            skSolve(sketch);
        }
        {
            var Q0;
            {var subQ0=sQuery(id+"F22.wireOp",EDGE,"E77");Q0=makeQuery(id+"F22.imprint","IMPRINT",FACE,{"disambiguationData":[TD([[makeQuery(id+"F22.imprint","IMPRINT",EDGE,{"derivedFrom":subQ0}),-1.0]])]});}
            var Q1;
            {var subQ0=sQuery(id+"F22.wireOp",EDGE,"E76");var subQ1=sQuery(id+"F16.wireOp",EDGE,"E57");var subQ2=sQuery(id+"F0.wireOp",EDGE,"E3");var subQ3=makeQuery(id+"F17.opExtrude","SWEPT_EDGE",EDGE,{"disambiguationData":[OSD([subQ2,subQ1,sQuery(id+"F16.wireOp",EDGE,"E58")])]});var subQ4=makeQuery(id+"F22.imprint","INTERSECT",VERTEX,{"derivedFrom":[subQ3,subQ0]});Q1=makeQuery(id+"F22.imprint","IMPRINT",FACE,{"disambiguationData":[TD([[makeQuery(id+"F22.imprint","IMPRINT",EDGE,{"disambiguationData":[TD([[subQ4,-1.0]])],"derivedFrom":subQ0}),1.0]])]});}
            var Q2;
            {var subQ0=sQuery(id+"F22.wireOp",EDGE,"E76");var subQ1=sQuery(id+"F16.wireOp",EDGE,"E69");var subQ2=sQuery(id+"F0.wireOp",EDGE,"E3");var subQ3=makeQuery(id+"F17.opExtrude","SWEPT_EDGE",EDGE,{"disambiguationData":[OSD([subQ2,subQ1,sQuery(id+"F16.wireOp",EDGE,"E72")])]});var subQ4=makeQuery(id+"F22.imprint","INTERSECT",VERTEX,{"derivedFrom":[subQ3,subQ0]});Q2=makeQuery(id+"F22.imprint","IMPRINT",FACE,{"disambiguationData":[TD([[makeQuery(id+"F22.imprint","IMPRINT",EDGE,{"disambiguationData":[TD([[subQ4,-1.0]])],"derivedFrom":subQ0}),1.0]])]});}
            var Q3;
            {var subQ0=sQuery(id+"F22.wireOp",EDGE,"E78");var subQ2=sQuery(id+"F16.wireOp",EDGE,"E41");var subQ3=sQuery(id+"F0.wireOp",EDGE,"E3");var subQ5=makeQuery(id+"F17.opExtrude","SWEPT_EDGE",EDGE,{"disambiguationData":[OSD([subQ3,subQ2,sQuery(id+"F16.wireOp",EDGE,"E47")])]});var subQ7=makeQuery(id+"F22.imprint","INTERSECT",VERTEX,{"derivedFrom":[subQ5,subQ0]});Q3=makeQuery(id+"F22.imprint","IMPRINT",FACE,{"disambiguationData":[TD([[makeQuery(id+"F22.imprint","IMPRINT",EDGE,{"disambiguationData":[TD([[subQ7,-1.0]])],"derivedFrom":subQ5}),-1.0]])]});}
            var Q4;
            Q4=makeQuery(id+"F17.opExtrude","SWEPT_FACE",FACE,{"disambiguationData":[OSD([sQuery(id+"F16.wireOp",EDGE,"E53")])]});
            extrude(context, id + "F23", {"entities" : qUnion([Q0, Q1, Q2, Q3]), "operationType" : NewBodyOperationType.REMOVE, "endBound" : BoundingType.UP_TO_SURFACE, "oppositeDirection" : true, "endBoundEntityFace" : qUnion([Q4]), "depth" : 25.4 * mm});
        }
        {
            var Q0;
            Q0=makeQuery(id+"F17.opExtrude","CAP_FACE",FACE,{"disambiguationData":[OSD([sQuery(id+"F16.wireOp",EDGE,"E37"),sQuery(id+"F16.wireOp",EDGE,"E38"),sQuery(id+"F16.wireOp",EDGE,"E43.0"),sQuery(id+"F16.wireOp",EDGE,"E43.1"),sQuery(id+"F16.wireOp",EDGE,"E53"),sQuery(id+"F16.wireOp",EDGE,"E54"),sQuery(id+"F16.wireOp",EDGE,"E55.bottom"),sQuery(id+"F16.wireOp",EDGE,"E55.top"),sQuery(id+"F16.wireOp",EDGE,"E55.right")])],"isStart":false});
            extrude(context, id + "F24", {"entities" : qUnion([Q0]), "operationType" : NewBodyOperationType.REMOVE, "oppositeDirection" : true, "depth" : 457.2 * mm});
        }
        {
            var Q0;
            {var subQ8=makeQuery(id+"F3.opExtrude","SWEPT_FACE",FACE,{"disambiguationData":[OSD([sQuery(id+"F2.wireOp",EDGE,"E16.top")])]});Q0=makeQuery(id+"F23.boolean.opBoolean","SPLIT",FACE,{"disambiguationData":[TD([subQ8])],"derivedFrom":makeQuery(id+"F15.boolean.opBoolean","SPLIT",FACE,{"disambiguationData":[TD([subQ8])],"derivedFrom":makeQuery(id+"F15.opExtrude","SWEPT_FACE",FACE,{"disambiguationData":[OSD([sQuery(id+"F14.wireOp",EDGE,"E35.top")])]})})});}
            var sketch = newSketch(context, id + "F25", { "sketchPlane" : qUnion([Q0])});
            skLineSegment(sketch, "E79", {"start": v(25.4, -1560.78) * mm, "end": v(25.4, -1478.38) * mm});
            skLineSegment(sketch, "E80", {"start": v(25.4, -1478.38) * mm, "end": v(0, -1501.54) * mm});
            skLineSegment(sketch, "E81", {"start": v(0, -1501.54) * mm, "end": v(0, -1589.81) * mm});
            skLineSegment(sketch, "E82", {"start": v(0, -1589.81) * mm, "end": v(25.4, -1560.78) * mm});
            skSolve(sketch);
        }
        {
            var Q0;
            Q0=makeQuery(id+"F25.imprint","IMPRINT",FACE,{"disambiguationData":[TD([[makeQuery(id+"F25.imprint","IMPRINT",EDGE,{"derivedFrom":sQuery(id+"F25.wireOp",EDGE,"E79")}),1.0]])]});
            var Q1;
            {var subQ1=sQuery(id+"F2.wireOp",EDGE,"E19");var subQ3=sQuery(id+"F2.wireOp",EDGE,"E18");var subQ5=sQuery(id+"F2.wireOp",EDGE,"E17.left");var subQ8=sQuery(id+"F2.wireOp",EDGE,"E6.left");var subQ10=sQuery(id+"F2.wireOp",EDGE,"E9.left");var subQ12=sQuery(id+"F2.wireOp",EDGE,"E24.MirrorCS");var subQ13=sQuery(id+"F2.wireOp",EDGE,"E21");var subQ15=sQuery(id+"F2.wireOp",EDGE,"E16.left");var subQ17=sQuery(id+"F2.wireOp",EDGE,"E16.right");var subQ19=sQuery(id+"F16.wireOp",EDGE,"E47");var subQ20=sQuery(id+"F16.wireOp",EDGE,"E41");var subQ21=sQuery(id+"F0.wireOp",EDGE,"E3");var subQ23=sQuery(id+"F16.wireOp",EDGE,"E46.0");var subQ24=sQuery(id+"F8.wireOp",EDGE,"E31.right");var subQ25=sQuery(id+"F2.wireOp",EDGE,"E8.left");var subQ27=sQuery(id+"F2.wireOp",EDGE,"E14.bottom");var subQ28=sQuery(id+"F16.wireOp",EDGE,"E42");var subQ29=sQuery(id+"F2.wireOp",EDGE,"E15.top");var subQ31=sQuery(id+"F16.wireOp",EDGE,"E50");var subQ32=sQuery(id+"F2.wireOp",EDGE,"E9.bottom");var subQ34=sQuery(id+"F0.wireOp",EDGE,"E0.bottom");var subQ35=sQuery(id+"F16.wireOp",EDGE,"E49");var subQ36=sQuery(id+"F2.wireOp",EDGE,"E13.top");var subQ37=sQuery(id+"F2.wireOp",EDGE,"E15.bottom");var subQ38=sQuery(id+"F2.wireOp",EDGE,"E14.top");var subQ39=sQuery(id+"F8.wireOp",EDGE,"E31.left");var subQ40=sQuery(id+"F8.wireOp",EDGE,"E32.right");var subQ41=sQuery(id+"F2.wireOp",EDGE,"E13.bottom");var subQ42=sQuery(id+"F2.wireOp",EDGE,"E12.top");var subQ43=sQuery(id+"F2.wireOp",EDGE,"E6.bottom");var subQ44=sQuery(id+"F2.wireOp",EDGE,"E8.top");var subQ45=sQuery(id+"F2.wireOp",EDGE,"E7.top");var subQ46=sQuery(id+"F2.wireOp",EDGE,"E6.top");var subQ47=sQuery(id+"F2.wireOp",EDGE,"E7.bottom");var subQ48=sQuery(id+"F2.wireOp",EDGE,"E7.left");var subQ49=sQuery(id+"F2.wireOp",EDGE,"E8.bottom");var subQ50=sQuery(id+"F2.wireOp",EDGE,"E9.top");var subQ51=sQuery(id+"F2.wireOp",EDGE,"E10.bottom");var subQ52=sQuery(id+"F2.wireOp",EDGE,"E11.top");var subQ53=sQuery(id+"F2.wireOp",EDGE,"E10.top");var subQ54=sQuery(id+"F2.wireOp",EDGE,"E12.bottom");var subQ55=sQuery(id+"F8.wireOp",EDGE,"E32.left");var subQ56=sQuery(id+"F2.wireOp",EDGE,"E11.bottom");Q1=makeQuery(id+"F23.boolean.opBoolean","SPLIT",FACE,{"disambiguationData":[TD([makeQuery(id+"F23.opExtrude","SWEPT_FACE",FACE,{"disambiguationData":[OSD([subQ21,subQ20,subQ19])]})])],"derivedFrom":makeQuery(id+"F19.boolean.opBoolean","SPLIT",FACE,{"disambiguationData":[TD([makeQuery(id+"F1.opExtrude","SWEPT_FACE",FACE,{"disambiguationData":[OSD([subQ34])]})])],"derivedFrom":makeQuery(id+"F17.boolean.opBoolean","MERGE",FACE,{"derivedFrom":[makeQuery(id+"F15.boolean.opBoolean","MERGE",FACE,{"derivedFrom":[makeQuery(id+"F3.opExtrude","CAP_FACE",FACE,{"disambiguationData":[OSD([sQuery(id+"F2.wireOp",EDGE,"E16.bottom"),sQuery(id+"F2.wireOp",EDGE,"E16.top"),subQ15,subQ17])],"isStart":false}),makeQuery(id+"F3.opExtrude","CAP_FACE",FACE,{"disambiguationData":[OSD([sQuery(id+"F2.wireOp",EDGE,"E17.bottom"),sQuery(id+"F2.wireOp",EDGE,"E17.top"),subQ5,subQ3])],"isStart":false}),makeQuery(id+"F3.opExtrude","CAP_FACE",FACE,{"disambiguationData":[OSD([subQ1,subQ13,sQuery(id+"F2.wireOp",EDGE,"E22"),sQuery(id+"F2.wireOp",EDGE,"E23.MirrorCS"),subQ12])],"isStart":false}),makeQuery(id+"F9.opExtrude","CAP_FACE",FACE,{"disambiguationData":[OSD([sQuery(id+"F8.wireOp",EDGE,"E31.bottom"),sQuery(id+"F8.wireOp",EDGE,"E31.top"),subQ39,subQ24])],"isStart":false}),makeQuery(id+"F9.opExtrude","CAP_FACE",FACE,{"disambiguationData":[OSD([sQuery(id+"F8.wireOp",EDGE,"E32.bottom"),sQuery(id+"F8.wireOp",EDGE,"E32.top"),subQ55,subQ40])],"isStart":false}),makeQuery(id+"F11.boolean.opBoolean","MERGE",FACE,{"derivedFrom":[makeQuery(id+"F3.opExtrude","CAP_FACE",FACE,{"disambiguationData":[OSD([subQ43,subQ46,subQ8,sQuery(id+"F2.wireOp",EDGE,"E6.right")])],"isStart":false}),makeQuery(id+"F3.opExtrude","CAP_FACE",FACE,{"disambiguationData":[OSD([subQ47,subQ45,subQ48,sQuery(id+"F2.wireOp",EDGE,"E7.right")])],"isStart":false}),makeQuery(id+"F3.opExtrude","CAP_FACE",FACE,{"disambiguationData":[OSD([subQ51,subQ53,sQuery(id+"F2.wireOp",EDGE,"E10.left"),sQuery(id+"F2.wireOp",EDGE,"E10.right")])],"isStart":false}),makeQuery(id+"F3.opExtrude","CAP_FACE",FACE,{"disambiguationData":[OSD([subQ56,subQ52,sQuery(id+"F2.wireOp",EDGE,"E11.left"),sQuery(id+"F2.wireOp",EDGE,"E11.right")])],"isStart":false}),makeQuery(id+"F11.opExtrude","SWEPT_FACE",FACE,{"disambiguationData":[OSD([sQuery(id+"F10.wireOp",EDGE,"E33.bottom")])]})]}),makeQuery(id+"F13.boolean.opBoolean","MERGE",FACE,{"derivedFrom":[makeQuery(id+"F3.opExtrude","CAP_FACE",FACE,{"disambiguationData":[OSD([subQ49,subQ44,subQ25,sQuery(id+"F2.wireOp",EDGE,"E8.right")])],"isStart":false}),makeQuery(id+"F3.opExtrude","CAP_FACE",FACE,{"disambiguationData":[OSD([subQ32,subQ50,subQ10,sQuery(id+"F2.wireOp",EDGE,"E9.right")])],"isStart":false}),makeQuery(id+"F3.opExtrude","CAP_FACE",FACE,{"disambiguationData":[OSD([subQ54,subQ42,sQuery(id+"F2.wireOp",EDGE,"E12.left"),sQuery(id+"F2.wireOp",EDGE,"E12.right")])],"isStart":false}),makeQuery(id+"F3.opExtrude","CAP_FACE",FACE,{"disambiguationData":[OSD([subQ41,subQ36,sQuery(id+"F2.wireOp",EDGE,"E13.left"),sQuery(id+"F2.wireOp",EDGE,"E13.right")])],"isStart":false}),makeQuery(id+"F3.opExtrude","CAP_FACE",FACE,{"disambiguationData":[OSD([subQ27,subQ38,sQuery(id+"F2.wireOp",EDGE,"E14.left"),sQuery(id+"F2.wireOp",EDGE,"E14.right")])],"isStart":false}),makeQuery(id+"F3.opExtrude","CAP_FACE",FACE,{"disambiguationData":[OSD([subQ37,subQ29,sQuery(id+"F2.wireOp",EDGE,"E15.left"),sQuery(id+"F2.wireOp",EDGE,"E15.right")])],"isStart":false}),makeQuery(id+"F13.opExtrude","SWEPT_FACE",FACE,{"disambiguationData":[OSD([sQuery(id+"F12.wireOp",EDGE,"E34.bottom")])]})]}),makeQuery(id+"F15.opExtrude","SWEPT_FACE",FACE,{"disambiguationData":[OSD([sQuery(id+"F14.wireOp",EDGE,"E35.bottom")])]}),makeQuery(id+"F15.opExtrude","SWEPT_FACE",FACE,{"disambiguationData":[OSD([sQuery(id+"F14.wireOp",EDGE,"E36.bottom")])]})]}),makeQuery(id+"F17.opExtrude","CAP_FACE",FACE,{"disambiguationData":[OSD([subQ20,subQ23,subQ19,sQuery(id+"F16.wireOp",EDGE,"E48")])],"isStart":false}),makeQuery(id+"F17.opExtrude","CAP_FACE",FACE,{"disambiguationData":[OSD([subQ28,sQuery(id+"F16.wireOp",EDGE,"E45.0"),subQ35,subQ31])],"isStart":false})]})})});}
            extrude(context, id + "F26", {"entities" : qUnion([Q0]), "operationType" : NewBodyOperationType.ADD, "endBound" : BoundingType.UP_TO_SURFACE, "oppositeDirection" : true, "endBoundEntityFace" : qUnion([Q1]), "depth" : 25.4 * mm});
        }
        {
            var Q0;
            {var subQ2=makeQuery(id+"F3.opExtrude","SWEPT_FACE",FACE,{"disambiguationData":[OSD([sQuery(id+"F2.wireOp",EDGE,"E23.MirrorCS")])]});Q0=makeQuery(id+"F19.boolean.opBoolean","SPLIT",FACE,{"disambiguationData":[TD([subQ2])],"derivedFrom":makeQuery(id+"F15.boolean.opBoolean","SPLIT",FACE,{"disambiguationData":[TD([makeQuery(id+"F3.opExtrude","SWEPT_FACE",FACE,{"disambiguationData":[OSD([sQuery(id+"F2.wireOp",EDGE,"E17.top")])]})])],"derivedFrom":makeQuery(id+"F15.opExtrude","SWEPT_FACE",FACE,{"disambiguationData":[OSD([sQuery(id+"F14.wireOp",EDGE,"E35.top")])]})})});}
            var sketch = newSketch(context, id + "F27", { "sketchPlane" : qUnion([Q0])});
            skLineSegment(sketch, "E83", {"start": v(25.4, -877.62) * mm, "end": v(25.4, -771.03) * mm});
            skLineSegment(sketch, "E84", {"start": v(25.4, -771.03) * mm, "end": v(0, -767.7) * mm});
            skLineSegment(sketch, "E85", {"start": v(0, -767.7) * mm, "end": v(0, -848.59) * mm});
            skLineSegment(sketch, "E86", {"start": v(0, -848.59) * mm, "end": v(25.4, -877.62) * mm});
            skSolve(sketch);
        }
        {
            var Q0;
            Q0=makeQuery(id+"F27.imprint","IMPRINT",FACE,{"disambiguationData":[TD([[makeQuery(id+"F27.imprint","IMPRINT",EDGE,{"derivedFrom":sQuery(id+"F27.wireOp",EDGE,"E83")}),1.0]])]});
            var Q1;
            {var subQ1=sQuery(id+"F2.wireOp",EDGE,"E19");var subQ3=sQuery(id+"F2.wireOp",EDGE,"E18");var subQ5=sQuery(id+"F2.wireOp",EDGE,"E17.left");var subQ8=sQuery(id+"F2.wireOp",EDGE,"E6.left");var subQ10=sQuery(id+"F2.wireOp",EDGE,"E9.left");var subQ12=sQuery(id+"F2.wireOp",EDGE,"E24.MirrorCS");var subQ13=sQuery(id+"F2.wireOp",EDGE,"E21");var subQ15=sQuery(id+"F2.wireOp",EDGE,"E16.left");var subQ17=sQuery(id+"F2.wireOp",EDGE,"E16.right");var subQ19=sQuery(id+"F16.wireOp",EDGE,"E47");var subQ20=sQuery(id+"F16.wireOp",EDGE,"E41");var subQ21=sQuery(id+"F0.wireOp",EDGE,"E3");var subQ23=sQuery(id+"F16.wireOp",EDGE,"E46.0");var subQ24=sQuery(id+"F8.wireOp",EDGE,"E31.right");var subQ25=sQuery(id+"F2.wireOp",EDGE,"E8.left");var subQ26=sQuery(id+"F16.wireOp",EDGE,"E61");var subQ27=sQuery(id+"F2.wireOp",EDGE,"E14.bottom");var subQ28=sQuery(id+"F16.wireOp",EDGE,"E42");var subQ29=sQuery(id+"F2.wireOp",EDGE,"E15.top");var subQ31=sQuery(id+"F16.wireOp",EDGE,"E50");var subQ32=sQuery(id+"F2.wireOp",EDGE,"E9.bottom");var subQ33=sQuery(id+"F0.wireOp",EDGE,"E5");var subQ34=sQuery(id+"F0.wireOp",EDGE,"E0.bottom");var subQ35=sQuery(id+"F16.wireOp",EDGE,"E49");var subQ36=sQuery(id+"F2.wireOp",EDGE,"E13.top");var subQ37=sQuery(id+"F2.wireOp",EDGE,"E15.bottom");var subQ38=sQuery(id+"F2.wireOp",EDGE,"E14.top");var subQ39=sQuery(id+"F8.wireOp",EDGE,"E31.left");var subQ40=sQuery(id+"F8.wireOp",EDGE,"E32.right");var subQ41=sQuery(id+"F2.wireOp",EDGE,"E13.bottom");var subQ42=sQuery(id+"F2.wireOp",EDGE,"E12.top");var subQ43=sQuery(id+"F2.wireOp",EDGE,"E6.bottom");var subQ44=sQuery(id+"F2.wireOp",EDGE,"E8.top");var subQ45=sQuery(id+"F2.wireOp",EDGE,"E7.top");var subQ46=sQuery(id+"F2.wireOp",EDGE,"E6.top");var subQ47=sQuery(id+"F2.wireOp",EDGE,"E7.bottom");var subQ48=sQuery(id+"F2.wireOp",EDGE,"E7.left");var subQ49=sQuery(id+"F2.wireOp",EDGE,"E8.bottom");var subQ50=sQuery(id+"F2.wireOp",EDGE,"E9.top");var subQ51=sQuery(id+"F2.wireOp",EDGE,"E10.bottom");var subQ52=sQuery(id+"F2.wireOp",EDGE,"E11.top");var subQ53=sQuery(id+"F2.wireOp",EDGE,"E10.top");var subQ54=sQuery(id+"F2.wireOp",EDGE,"E12.bottom");var subQ55=makeQuery(id+"F19.opExtrude","SWEPT_FACE",FACE,{"disambiguationData":[OSD([subQ33,subQ26,sQuery(id+"F16.wireOp",EDGE,"E62")])]});var subQ56=sQuery(id+"F8.wireOp",EDGE,"E32.left");var subQ57=sQuery(id+"F2.wireOp",EDGE,"E11.bottom");var subQ58=makeQuery(id+"F19.boolean.opBoolean","SPLIT",FACE,{"disambiguationData":[TD([makeQuery(id+"F1.opExtrude","SWEPT_FACE",FACE,{"disambiguationData":[OSD([subQ34])]})])],"derivedFrom":makeQuery(id+"F17.boolean.opBoolean","MERGE",FACE,{"derivedFrom":[makeQuery(id+"F15.boolean.opBoolean","MERGE",FACE,{"derivedFrom":[makeQuery(id+"F3.opExtrude","CAP_FACE",FACE,{"disambiguationData":[OSD([sQuery(id+"F2.wireOp",EDGE,"E16.bottom"),sQuery(id+"F2.wireOp",EDGE,"E16.top"),subQ15,subQ17])],"isStart":false}),makeQuery(id+"F3.opExtrude","CAP_FACE",FACE,{"disambiguationData":[OSD([sQuery(id+"F2.wireOp",EDGE,"E17.bottom"),sQuery(id+"F2.wireOp",EDGE,"E17.top"),subQ5,subQ3])],"isStart":false}),makeQuery(id+"F3.opExtrude","CAP_FACE",FACE,{"disambiguationData":[OSD([subQ1,subQ13,sQuery(id+"F2.wireOp",EDGE,"E22"),sQuery(id+"F2.wireOp",EDGE,"E23.MirrorCS"),subQ12])],"isStart":false}),makeQuery(id+"F9.opExtrude","CAP_FACE",FACE,{"disambiguationData":[OSD([sQuery(id+"F8.wireOp",EDGE,"E31.bottom"),sQuery(id+"F8.wireOp",EDGE,"E31.top"),subQ39,subQ24])],"isStart":false}),makeQuery(id+"F9.opExtrude","CAP_FACE",FACE,{"disambiguationData":[OSD([sQuery(id+"F8.wireOp",EDGE,"E32.bottom"),sQuery(id+"F8.wireOp",EDGE,"E32.top"),subQ56,subQ40])],"isStart":false}),makeQuery(id+"F11.boolean.opBoolean","MERGE",FACE,{"derivedFrom":[makeQuery(id+"F3.opExtrude","CAP_FACE",FACE,{"disambiguationData":[OSD([subQ43,subQ46,subQ8,sQuery(id+"F2.wireOp",EDGE,"E6.right")])],"isStart":false}),makeQuery(id+"F3.opExtrude","CAP_FACE",FACE,{"disambiguationData":[OSD([subQ47,subQ45,subQ48,sQuery(id+"F2.wireOp",EDGE,"E7.right")])],"isStart":false}),makeQuery(id+"F3.opExtrude","CAP_FACE",FACE,{"disambiguationData":[OSD([subQ51,subQ53,sQuery(id+"F2.wireOp",EDGE,"E10.left"),sQuery(id+"F2.wireOp",EDGE,"E10.right")])],"isStart":false}),makeQuery(id+"F3.opExtrude","CAP_FACE",FACE,{"disambiguationData":[OSD([subQ57,subQ52,sQuery(id+"F2.wireOp",EDGE,"E11.left"),sQuery(id+"F2.wireOp",EDGE,"E11.right")])],"isStart":false}),makeQuery(id+"F11.opExtrude","SWEPT_FACE",FACE,{"disambiguationData":[OSD([sQuery(id+"F10.wireOp",EDGE,"E33.bottom")])]})]}),makeQuery(id+"F13.boolean.opBoolean","MERGE",FACE,{"derivedFrom":[makeQuery(id+"F3.opExtrude","CAP_FACE",FACE,{"disambiguationData":[OSD([subQ49,subQ44,subQ25,sQuery(id+"F2.wireOp",EDGE,"E8.right")])],"isStart":false}),makeQuery(id+"F3.opExtrude","CAP_FACE",FACE,{"disambiguationData":[OSD([subQ32,subQ50,subQ10,sQuery(id+"F2.wireOp",EDGE,"E9.right")])],"isStart":false}),makeQuery(id+"F3.opExtrude","CAP_FACE",FACE,{"disambiguationData":[OSD([subQ54,subQ42,sQuery(id+"F2.wireOp",EDGE,"E12.left"),sQuery(id+"F2.wireOp",EDGE,"E12.right")])],"isStart":false}),makeQuery(id+"F3.opExtrude","CAP_FACE",FACE,{"disambiguationData":[OSD([subQ41,subQ36,sQuery(id+"F2.wireOp",EDGE,"E13.left"),sQuery(id+"F2.wireOp",EDGE,"E13.right")])],"isStart":false}),makeQuery(id+"F3.opExtrude","CAP_FACE",FACE,{"disambiguationData":[OSD([subQ27,subQ38,sQuery(id+"F2.wireOp",EDGE,"E14.left"),sQuery(id+"F2.wireOp",EDGE,"E14.right")])],"isStart":false}),makeQuery(id+"F3.opExtrude","CAP_FACE",FACE,{"disambiguationData":[OSD([subQ37,subQ29,sQuery(id+"F2.wireOp",EDGE,"E15.left"),sQuery(id+"F2.wireOp",EDGE,"E15.right")])],"isStart":false}),makeQuery(id+"F13.opExtrude","SWEPT_FACE",FACE,{"disambiguationData":[OSD([sQuery(id+"F12.wireOp",EDGE,"E34.bottom")])]})]}),makeQuery(id+"F15.opExtrude","SWEPT_FACE",FACE,{"disambiguationData":[OSD([sQuery(id+"F14.wireOp",EDGE,"E35.bottom")])]}),makeQuery(id+"F15.opExtrude","SWEPT_FACE",FACE,{"disambiguationData":[OSD([sQuery(id+"F14.wireOp",EDGE,"E36.bottom")])]})]}),makeQuery(id+"F17.opExtrude","CAP_FACE",FACE,{"disambiguationData":[OSD([subQ20,subQ23,subQ19,sQuery(id+"F16.wireOp",EDGE,"E48")])],"isStart":false}),makeQuery(id+"F17.opExtrude","CAP_FACE",FACE,{"disambiguationData":[OSD([subQ28,sQuery(id+"F16.wireOp",EDGE,"E45.0"),subQ35,subQ31])],"isStart":false})]})});Q1=makeQuery(id+"F26.boolean.opBoolean","MERGE",FACE,{"derivedFrom":[makeQuery(id+"F23.boolean.opBoolean","SPLIT",FACE,{"disambiguationData":[TD([makeQuery(id+"F19.boolean.opBoolean","COPY",FACE,{"derivedFrom":subQ55})])],"derivedFrom":subQ58}),makeQuery(id+"F23.boolean.opBoolean","SPLIT",FACE,{"disambiguationData":[TD([makeQuery(id+"F23.opExtrude","SWEPT_FACE",FACE,{"disambiguationData":[OSD([subQ21,subQ20,subQ19])]})])],"derivedFrom":subQ58}),makeQuery(id+"F26.opExtrude","CAP_FACE",FACE,{"disambiguationData":[OSD([sQuery(id+"F25.wireOp",EDGE,"E79"),sQuery(id+"F25.wireOp",EDGE,"E80"),sQuery(id+"F25.wireOp",EDGE,"E81"),sQuery(id+"F25.wireOp",EDGE,"E82")])],"isStart":false})]});}
            extrude(context, id + "F28", {"entities" : qUnion([Q0]), "operationType" : NewBodyOperationType.ADD, "endBound" : BoundingType.UP_TO_SURFACE, "oppositeDirection" : true, "endBoundEntityFace" : qUnion([Q1]), "depth" : 25.4 * mm});
        }
        {
            var Q0;
            {var subQ1=sQuery(id+"F2.wireOp",EDGE,"E19");var subQ3=sQuery(id+"F2.wireOp",EDGE,"E18");var subQ5=sQuery(id+"F2.wireOp",EDGE,"E17.left");var subQ8=sQuery(id+"F2.wireOp",EDGE,"E6.left");var subQ10=sQuery(id+"F2.wireOp",EDGE,"E9.left");var subQ12=sQuery(id+"F2.wireOp",EDGE,"E24.MirrorCS");var subQ13=sQuery(id+"F2.wireOp",EDGE,"E21");var subQ15=sQuery(id+"F2.wireOp",EDGE,"E16.left");var subQ17=sQuery(id+"F2.wireOp",EDGE,"E16.right");var subQ19=sQuery(id+"F16.wireOp",EDGE,"E47");var subQ20=sQuery(id+"F16.wireOp",EDGE,"E41");var subQ21=sQuery(id+"F0.wireOp",EDGE,"E3");var subQ23=sQuery(id+"F16.wireOp",EDGE,"E46.0");var subQ24=sQuery(id+"F8.wireOp",EDGE,"E31.right");var subQ25=sQuery(id+"F2.wireOp",EDGE,"E8.left");var subQ26=sQuery(id+"F16.wireOp",EDGE,"E61");var subQ27=sQuery(id+"F2.wireOp",EDGE,"E14.bottom");var subQ28=sQuery(id+"F16.wireOp",EDGE,"E42");var subQ29=sQuery(id+"F2.wireOp",EDGE,"E15.top");var subQ31=sQuery(id+"F16.wireOp",EDGE,"E50");var subQ32=sQuery(id+"F2.wireOp",EDGE,"E9.bottom");var subQ33=sQuery(id+"F0.wireOp",EDGE,"E5");var subQ34=sQuery(id+"F0.wireOp",EDGE,"E0.bottom");var subQ35=sQuery(id+"F16.wireOp",EDGE,"E49");var subQ36=sQuery(id+"F2.wireOp",EDGE,"E13.top");var subQ37=sQuery(id+"F2.wireOp",EDGE,"E15.bottom");var subQ38=sQuery(id+"F2.wireOp",EDGE,"E14.top");var subQ39=sQuery(id+"F8.wireOp",EDGE,"E31.left");var subQ40=sQuery(id+"F8.wireOp",EDGE,"E32.right");var subQ41=sQuery(id+"F2.wireOp",EDGE,"E13.bottom");var subQ42=sQuery(id+"F2.wireOp",EDGE,"E12.top");var subQ43=sQuery(id+"F2.wireOp",EDGE,"E6.bottom");var subQ44=sQuery(id+"F2.wireOp",EDGE,"E8.top");var subQ45=sQuery(id+"F2.wireOp",EDGE,"E7.top");var subQ46=sQuery(id+"F2.wireOp",EDGE,"E6.top");var subQ47=sQuery(id+"F2.wireOp",EDGE,"E7.bottom");var subQ48=sQuery(id+"F2.wireOp",EDGE,"E7.left");var subQ49=sQuery(id+"F2.wireOp",EDGE,"E8.bottom");var subQ50=sQuery(id+"F2.wireOp",EDGE,"E9.top");var subQ51=sQuery(id+"F2.wireOp",EDGE,"E10.bottom");var subQ52=sQuery(id+"F2.wireOp",EDGE,"E11.top");var subQ53=sQuery(id+"F2.wireOp",EDGE,"E10.top");var subQ54=sQuery(id+"F2.wireOp",EDGE,"E12.bottom");var subQ55=makeQuery(id+"F19.opExtrude","SWEPT_FACE",FACE,{"disambiguationData":[OSD([subQ33,subQ26,sQuery(id+"F16.wireOp",EDGE,"E62")])]});var subQ56=sQuery(id+"F8.wireOp",EDGE,"E32.left");var subQ57=sQuery(id+"F2.wireOp",EDGE,"E11.bottom");var subQ58=makeQuery(id+"F17.boolean.opBoolean","MERGE",FACE,{"derivedFrom":[makeQuery(id+"F15.boolean.opBoolean","MERGE",FACE,{"derivedFrom":[makeQuery(id+"F3.opExtrude","CAP_FACE",FACE,{"disambiguationData":[OSD([sQuery(id+"F2.wireOp",EDGE,"E16.bottom"),sQuery(id+"F2.wireOp",EDGE,"E16.top"),subQ15,subQ17])],"isStart":false}),makeQuery(id+"F3.opExtrude","CAP_FACE",FACE,{"disambiguationData":[OSD([sQuery(id+"F2.wireOp",EDGE,"E17.bottom"),sQuery(id+"F2.wireOp",EDGE,"E17.top"),subQ5,subQ3])],"isStart":false}),makeQuery(id+"F3.opExtrude","CAP_FACE",FACE,{"disambiguationData":[OSD([subQ1,subQ13,sQuery(id+"F2.wireOp",EDGE,"E22"),sQuery(id+"F2.wireOp",EDGE,"E23.MirrorCS"),subQ12])],"isStart":false}),makeQuery(id+"F9.opExtrude","CAP_FACE",FACE,{"disambiguationData":[OSD([sQuery(id+"F8.wireOp",EDGE,"E31.bottom"),sQuery(id+"F8.wireOp",EDGE,"E31.top"),subQ39,subQ24])],"isStart":false}),makeQuery(id+"F9.opExtrude","CAP_FACE",FACE,{"disambiguationData":[OSD([sQuery(id+"F8.wireOp",EDGE,"E32.bottom"),sQuery(id+"F8.wireOp",EDGE,"E32.top"),subQ56,subQ40])],"isStart":false}),makeQuery(id+"F11.boolean.opBoolean","MERGE",FACE,{"derivedFrom":[makeQuery(id+"F3.opExtrude","CAP_FACE",FACE,{"disambiguationData":[OSD([subQ43,subQ46,subQ8,sQuery(id+"F2.wireOp",EDGE,"E6.right")])],"isStart":false}),makeQuery(id+"F3.opExtrude","CAP_FACE",FACE,{"disambiguationData":[OSD([subQ47,subQ45,subQ48,sQuery(id+"F2.wireOp",EDGE,"E7.right")])],"isStart":false}),makeQuery(id+"F3.opExtrude","CAP_FACE",FACE,{"disambiguationData":[OSD([subQ51,subQ53,sQuery(id+"F2.wireOp",EDGE,"E10.left"),sQuery(id+"F2.wireOp",EDGE,"E10.right")])],"isStart":false}),makeQuery(id+"F3.opExtrude","CAP_FACE",FACE,{"disambiguationData":[OSD([subQ57,subQ52,sQuery(id+"F2.wireOp",EDGE,"E11.left"),sQuery(id+"F2.wireOp",EDGE,"E11.right")])],"isStart":false}),makeQuery(id+"F11.opExtrude","SWEPT_FACE",FACE,{"disambiguationData":[OSD([sQuery(id+"F10.wireOp",EDGE,"E33.bottom")])]})]}),makeQuery(id+"F13.boolean.opBoolean","MERGE",FACE,{"derivedFrom":[makeQuery(id+"F3.opExtrude","CAP_FACE",FACE,{"disambiguationData":[OSD([subQ49,subQ44,subQ25,sQuery(id+"F2.wireOp",EDGE,"E8.right")])],"isStart":false}),makeQuery(id+"F3.opExtrude","CAP_FACE",FACE,{"disambiguationData":[OSD([subQ32,subQ50,subQ10,sQuery(id+"F2.wireOp",EDGE,"E9.right")])],"isStart":false}),makeQuery(id+"F3.opExtrude","CAP_FACE",FACE,{"disambiguationData":[OSD([subQ54,subQ42,sQuery(id+"F2.wireOp",EDGE,"E12.left"),sQuery(id+"F2.wireOp",EDGE,"E12.right")])],"isStart":false}),makeQuery(id+"F3.opExtrude","CAP_FACE",FACE,{"disambiguationData":[OSD([subQ41,subQ36,sQuery(id+"F2.wireOp",EDGE,"E13.left"),sQuery(id+"F2.wireOp",EDGE,"E13.right")])],"isStart":false}),makeQuery(id+"F3.opExtrude","CAP_FACE",FACE,{"disambiguationData":[OSD([subQ27,subQ38,sQuery(id+"F2.wireOp",EDGE,"E14.left"),sQuery(id+"F2.wireOp",EDGE,"E14.right")])],"isStart":false}),makeQuery(id+"F3.opExtrude","CAP_FACE",FACE,{"disambiguationData":[OSD([subQ37,subQ29,sQuery(id+"F2.wireOp",EDGE,"E15.left"),sQuery(id+"F2.wireOp",EDGE,"E15.right")])],"isStart":false}),makeQuery(id+"F13.opExtrude","SWEPT_FACE",FACE,{"disambiguationData":[OSD([sQuery(id+"F12.wireOp",EDGE,"E34.bottom")])]})]}),makeQuery(id+"F15.opExtrude","SWEPT_FACE",FACE,{"disambiguationData":[OSD([sQuery(id+"F14.wireOp",EDGE,"E35.bottom")])]}),makeQuery(id+"F15.opExtrude","SWEPT_FACE",FACE,{"disambiguationData":[OSD([sQuery(id+"F14.wireOp",EDGE,"E36.bottom")])]})]}),makeQuery(id+"F17.opExtrude","CAP_FACE",FACE,{"disambiguationData":[OSD([subQ20,subQ23,subQ19,sQuery(id+"F16.wireOp",EDGE,"E48")])],"isStart":false}),makeQuery(id+"F17.opExtrude","CAP_FACE",FACE,{"disambiguationData":[OSD([subQ28,sQuery(id+"F16.wireOp",EDGE,"E45.0"),subQ35,subQ31])],"isStart":false})]});var subQ59=makeQuery(id+"F19.boolean.opBoolean","SPLIT",FACE,{"disambiguationData":[TD([makeQuery(id+"F1.opExtrude","SWEPT_FACE",FACE,{"disambiguationData":[OSD([subQ34])]})])],"derivedFrom":subQ58});Q0=makeQuery(id+"F28.boolean.opBoolean","MERGE",FACE,{"derivedFrom":[makeQuery(id+"F19.boolean.opBoolean","SPLIT",FACE,{"disambiguationData":[TD([makeQuery(id+"F19.opExtrude","SWEPT_FACE",FACE,{"disambiguationData":[OSD([subQ33,subQ28,subQ35])]})])],"derivedFrom":subQ58}),makeQuery(id+"F26.boolean.opBoolean","MERGE",FACE,{"derivedFrom":[makeQuery(id+"F23.boolean.opBoolean","SPLIT",FACE,{"disambiguationData":[TD([makeQuery(id+"F19.boolean.opBoolean","COPY",FACE,{"derivedFrom":subQ55})])],"derivedFrom":subQ59}),makeQuery(id+"F23.boolean.opBoolean","SPLIT",FACE,{"disambiguationData":[TD([makeQuery(id+"F23.opExtrude","SWEPT_FACE",FACE,{"disambiguationData":[OSD([subQ21,subQ20,subQ19])]})])],"derivedFrom":subQ59}),makeQuery(id+"F26.opExtrude","CAP_FACE",FACE,{"disambiguationData":[OSD([sQuery(id+"F25.wireOp",EDGE,"E79"),sQuery(id+"F25.wireOp",EDGE,"E80"),sQuery(id+"F25.wireOp",EDGE,"E81"),sQuery(id+"F25.wireOp",EDGE,"E82")])],"isStart":false})]}),makeQuery(id+"F28.opExtrude","CAP_FACE",FACE,{"disambiguationData":[OSD([sQuery(id+"F27.wireOp",EDGE,"E83"),sQuery(id+"F27.wireOp",EDGE,"E84"),sQuery(id+"F27.wireOp",EDGE,"E85"),sQuery(id+"F27.wireOp",EDGE,"E86")])],"isStart":false})]});}
            var sketch = newSketch(context, id + "F29", { "sketchPlane" : qUnion([Q0])});
            skLineSegment(sketch, "E87", {"start": v(0, 77.14) * mm, "end": v(0, 0) * mm});
            skLineSegment(sketch, "E88", {"start": v(0, 0) * mm, "end": v(25.4, 29.03) * mm});
            skLineSegment(sketch, "E89", {"start": v(25.4, 29.03) * mm, "end": v(25.4, 106.17) * mm});
            skLineSegment(sketch, "E90", {"start": v(25.4, 2332.23) * mm, "end": v(25.4, 2409.5) * mm});
            skLineSegment(sketch, "E91", {"start": v(25.4, 2409.5) * mm, "end": v(0, 2438.44) * mm});
            skLineSegment(sketch, "E92", {"start": v(0, 2438.44) * mm, "end": v(0, 2361.26) * mm});
            skLineSegment(sketch, "E93", {"start": v(0, 2361.26) * mm, "end": v(25.4, 2332.23) * mm});
            skLineSegment(sketch, "E94", {"start": v(0, 2438.4) * mm, "end": v(25.4, 2409.37) * mm});
            skSolve(sketch);
        }
        {
            var Q0;
            Q0=makeQuery(id+"F29.imprint","IMPRINT",FACE,{"disambiguationData":[TD([[makeQuery(id+"F29.imprint","IMPRINT",EDGE,{"derivedFrom":sQuery(id+"F29.wireOp",EDGE,"E87")}),1.0]])]});
            var Q1;
            {var subQ0=sQuery(id+"F29.wireOp",EDGE,"E93");Q1=makeQuery(id+"F29.imprint","IMPRINT",FACE,{"disambiguationData":[TD([[makeQuery(id+"F29.imprint","IMPRINT",EDGE,{"derivedFrom":subQ0}),-1.0]])]});}
            var Q2;
            {var subQ0=sQuery(id+"F18.wireOp",EDGE,"E73");var subQ1=sQuery(id+"F16.wireOp",EDGE,"E42");var subQ2=sQuery(id+"F0.wireOp",EDGE,"E5");Q2=makeQuery(id+"F19.boolean.opBoolean","COPY",FACE,{"derivedFrom":makeQuery(id+"F19.opExtrude","SWEPT_FACE",FACE,{"disambiguationData":[OSD([subQ0]),TDD([makeQuery(id+"F18.imprint","IMPRINT",EDGE,{"disambiguationData":[TD([[makeQuery(id+"F18.imprint","INTERSECT",VERTEX,{"derivedFrom":[makeQuery(id+"F17.opExtrude","SWEPT_EDGE",EDGE,{"disambiguationData":[OSD([subQ2,subQ1,sQuery(id+"F16.wireOp",EDGE,"E49")])]}),subQ0]}),1.0]])],"derivedFrom":subQ0})])]})});}
            extrude(context, id + "F30", {"entities" : qUnion([Q0, Q1]), "operationType" : NewBodyOperationType.ADD, "endBound" : BoundingType.UP_TO_SURFACE, "oppositeDirection" : true, "endBoundEntityFace" : qUnion([Q2]), "depth" : 25.4 * mm});
        }
        {
            var Q0;
            Q0=makeQuery(id+"F17.boolean.opBoolean","MERGE",FACE,{"derivedFrom":[makeQuery(id+"F1.opExtrude","SWEPT_FACE",FACE,{"disambiguationData":[OSD([sQuery(id+"F0.wireOp",EDGE,"E5")])]}),makeQuery(id+"F17.opExtrude","SWEPT_FACE",FACE,{"disambiguationData":[OSD([sQuery(id+"F16.wireOp",EDGE,"E40")])]}),makeQuery(id+"F17.opExtrude","SWEPT_FACE",FACE,{"disambiguationData":[OSD([sQuery(id+"F16.wireOp",EDGE,"E42")])]}),makeQuery(id+"F17.opExtrude","SWEPT_FACE",FACE,{"disambiguationData":[OSD([sQuery(id+"F16.wireOp",EDGE,"E61")])]}),makeQuery(id+"F17.opExtrude","SWEPT_FACE",FACE,{"disambiguationData":[OSD([sQuery(id+"F16.wireOp",EDGE,"E65")])]})]});
            var sketch = newSketch(context, id + "F31", { "sketchPlane" : qUnion([Q0])});
            skLineSegment(sketch, "E95", {"start": v(-1620.03, 1543.05) * mm, "end": v(0, 2000.25) * mm});
            skLineSegment(sketch, "E96.0", {"start": v(-1620.03, 1490.27) * mm, "end": v(0, 1947.47) * mm});
            skLineSegment(sketch, "E97", {"start": v(-1620.03, 1543.05) * mm, "end": v(-1620.03, 1490.27) * mm});
            skLineSegment(sketch, "E98", {"start": v(0, 2000.25) * mm, "end": v(0, 1947.47) * mm});
            skSolve(sketch);
        }
        {
            var Q0;
            {var subQ0=sQuery(id+"F31.wireOp",EDGE,"E95");var subQ1=sQuery(id+"F0.wireOp",EDGE,"E5");var subQ2=makeQuery(id+"F17.opExtrude","SWEPT_EDGE",EDGE,{"disambiguationData":[OSD([subQ1,sQuery(id+"F16.wireOp",EDGE,"E65"),sQuery(id+"F16.wireOp",EDGE,"E66")])]});var subQ3=makeQuery(id+"F31.imprint","INTERSECT",VERTEX,{"derivedFrom":[subQ2,subQ0]});var subQ4=makeQuery(id+"F17.opExtrude","SWEPT_EDGE",EDGE,{"disambiguationData":[OSD([subQ1,sQuery(id+"F16.wireOp",EDGE,"E40"),sQuery(id+"F16.wireOp",EDGE,"E52")])]});var subQ5=makeQuery(id+"F31.imprint","INTERSECT",VERTEX,{"derivedFrom":[subQ4,subQ0]});Q0=makeQuery(id+"F31.imprint","IMPRINT",FACE,{"disambiguationData":[TD([[makeQuery(id+"F31.imprint","IMPRINT",EDGE,{"disambiguationData":[TD([[subQ3,1.0],[subQ5,-1.0]])],"derivedFrom":subQ0}),-1.0]])]});}
            var Q1;
            {var subQ5=sQuery(id+"F31.wireOp",EDGE,"E97");Q1=makeQuery(id+"F31.imprint","IMPRINT",FACE,{"disambiguationData":[TD([[makeQuery(id+"F31.imprint","IMPRINT",EDGE,{"derivedFrom":subQ5}),1.0]])]});}
            var Q2;
            {var subQ0=sQuery(id+"F31.wireOp",EDGE,"E95");var subQ1=sQuery(id+"F0.wireOp",EDGE,"E5");var subQ2=makeQuery(id+"F17.opExtrude","SWEPT_EDGE",EDGE,{"disambiguationData":[OSD([subQ1,sQuery(id+"F16.wireOp",EDGE,"E61"),sQuery(id+"F16.wireOp",EDGE,"E62")])]});var subQ3=makeQuery(id+"F31.imprint","INTERSECT",VERTEX,{"derivedFrom":[subQ2,subQ0]});var subQ4=makeQuery(id+"F17.opExtrude","SWEPT_EDGE",EDGE,{"disambiguationData":[OSD([subQ1,sQuery(id+"F16.wireOp",EDGE,"E65"),sQuery(id+"F16.wireOp",EDGE,"E68")])]});var subQ5=makeQuery(id+"F31.imprint","INTERSECT",VERTEX,{"derivedFrom":[subQ4,subQ0]});Q2=makeQuery(id+"F31.imprint","IMPRINT",FACE,{"disambiguationData":[TD([[makeQuery(id+"F31.imprint","IMPRINT",EDGE,{"disambiguationData":[TD([[subQ3,1.0],[subQ5,-1.0]])],"derivedFrom":subQ0}),-1.0]])]});}
            var Q3;
            {var subQ0=sQuery(id+"F31.wireOp",EDGE,"E95");var subQ1=sQuery(id+"F16.wireOp",EDGE,"E65");var subQ2=sQuery(id+"F0.wireOp",EDGE,"E5");var subQ3=makeQuery(id+"F17.opExtrude","SWEPT_EDGE",EDGE,{"disambiguationData":[OSD([subQ2,subQ1,sQuery(id+"F16.wireOp",EDGE,"E68")])]});var subQ4=makeQuery(id+"F31.imprint","INTERSECT",VERTEX,{"derivedFrom":[subQ3,subQ0]});var subQ5=makeQuery(id+"F17.opExtrude","SWEPT_EDGE",EDGE,{"disambiguationData":[OSD([subQ2,subQ1,sQuery(id+"F16.wireOp",EDGE,"E66")])]});var subQ6=makeQuery(id+"F31.imprint","INTERSECT",VERTEX,{"derivedFrom":[subQ5,subQ0]});Q3=makeQuery(id+"F31.imprint","IMPRINT",FACE,{"disambiguationData":[TD([[makeQuery(id+"F31.imprint","IMPRINT",EDGE,{"disambiguationData":[TD([[subQ4,-1.0],[subQ6,1.0]])],"derivedFrom":subQ0}),1.0]])]});}
            var Q4;
            {var subQ0=sQuery(id+"F31.wireOp",EDGE,"E95");var subQ1=sQuery(id+"F16.wireOp",EDGE,"E61");var subQ2=sQuery(id+"F0.wireOp",EDGE,"E5");var subQ3=makeQuery(id+"F17.opExtrude","SWEPT_EDGE",EDGE,{"disambiguationData":[OSD([subQ2,subQ1,sQuery(id+"F16.wireOp",EDGE,"E64")])]});var subQ4=makeQuery(id+"F31.imprint","INTERSECT",VERTEX,{"derivedFrom":[subQ3,subQ0]});var subQ5=makeQuery(id+"F17.opExtrude","SWEPT_EDGE",EDGE,{"disambiguationData":[OSD([subQ2,subQ1,sQuery(id+"F16.wireOp",EDGE,"E62")])]});var subQ6=makeQuery(id+"F31.imprint","INTERSECT",VERTEX,{"derivedFrom":[subQ5,subQ0]});Q4=makeQuery(id+"F31.imprint","IMPRINT",FACE,{"disambiguationData":[TD([[makeQuery(id+"F31.imprint","IMPRINT",EDGE,{"disambiguationData":[TD([[subQ4,-1.0],[subQ6,1.0]])],"derivedFrom":subQ0}),1.0]])]});}
            var Q5;
            {var subQ0=sQuery(id+"F31.wireOp",EDGE,"E95");var subQ1=sQuery(id+"F0.wireOp",EDGE,"E5");var subQ2=makeQuery(id+"F17.opExtrude","SWEPT_EDGE",EDGE,{"disambiguationData":[OSD([subQ1,sQuery(id+"F16.wireOp",EDGE,"E42"),sQuery(id+"F16.wireOp",EDGE,"E49")])]});var subQ3=makeQuery(id+"F31.imprint","INTERSECT",VERTEX,{"derivedFrom":[subQ2,subQ0]});var subQ4=makeQuery(id+"F17.opExtrude","SWEPT_EDGE",EDGE,{"disambiguationData":[OSD([subQ1,sQuery(id+"F16.wireOp",EDGE,"E61"),sQuery(id+"F16.wireOp",EDGE,"E64")])]});var subQ5=makeQuery(id+"F31.imprint","INTERSECT",VERTEX,{"derivedFrom":[subQ4,subQ0]});Q5=makeQuery(id+"F31.imprint","IMPRINT",FACE,{"disambiguationData":[TD([[makeQuery(id+"F31.imprint","IMPRINT",EDGE,{"disambiguationData":[TD([[subQ3,1.0],[subQ5,-1.0]])],"derivedFrom":subQ0}),-1.0]])]});}
            var Q6;
            {var subQ5=sQuery(id+"F31.wireOp",EDGE,"E98");Q6=makeQuery(id+"F31.imprint","IMPRINT",FACE,{"disambiguationData":[TD([[makeQuery(id+"F31.imprint","IMPRINT",EDGE,{"derivedFrom":subQ5}),-1.0]])]});}
            extrude(context, id + "F32", {"entities" : qUnion([Q0, Q1, Q2, Q3, Q4, Q5, Q6]), "operationType" : NewBodyOperationType.ADD, "oppositeDirection" : true, "depth" : 25.4 * mm});
        }
        {
            var Q0;
            Q0=makeQuery(id+"F17.boolean.opBoolean","MERGE",FACE,{"derivedFrom":[makeQuery(id+"F1.opExtrude","SWEPT_FACE",FACE,{"disambiguationData":[OSD([sQuery(id+"F0.wireOp",EDGE,"E3")])]}),makeQuery(id+"F17.opExtrude","SWEPT_FACE",FACE,{"disambiguationData":[OSD([sQuery(id+"F16.wireOp",EDGE,"E37")])]}),makeQuery(id+"F17.opExtrude","SWEPT_FACE",FACE,{"disambiguationData":[OSD([sQuery(id+"F16.wireOp",EDGE,"E41")])]}),makeQuery(id+"F17.opExtrude","SWEPT_FACE",FACE,{"disambiguationData":[OSD([sQuery(id+"F16.wireOp",EDGE,"E57")])]}),makeQuery(id+"F17.opExtrude","SWEPT_FACE",FACE,{"disambiguationData":[OSD([sQuery(id+"F16.wireOp",EDGE,"E69")])]})]});
            var sketch = newSketch(context, id + "F33", { "sketchPlane" : qUnion([Q0])});
            skLineSegment(sketch, "E99", {"start": v(-1605.7, 2000.25) * mm, "end": v(14.34, 1543.05) * mm});
            skLineSegment(sketch, "E100.0", {"start": v(-1605.7, 1947.47) * mm, "end": v(14.34, 1490.27) * mm});
            skLineSegment(sketch, "E101", {"start": v(-1605.7, 2000.25) * mm, "end": v(-1605.7, 1947.47) * mm});
            skLineSegment(sketch, "E102", {"start": v(14.34, 1543.05) * mm, "end": v(14.34, 1490.27) * mm});
            skSolve(sketch);
        }
        {
            var Q0;
            {var subQ5=sQuery(id+"F33.wireOp",EDGE,"E102");Q0=makeQuery(id+"F33.imprint","IMPRINT",FACE,{"disambiguationData":[TD([[makeQuery(id+"F33.imprint","IMPRINT",EDGE,{"derivedFrom":subQ5}),-1.0]])]});}
            var Q1;
            {var subQ0=sQuery(id+"F33.wireOp",EDGE,"E99");var subQ1=sQuery(id+"F0.wireOp",EDGE,"E3");var subQ2=makeQuery(id+"F17.opExtrude","SWEPT_EDGE",EDGE,{"disambiguationData":[OSD([subQ1,sQuery(id+"F16.wireOp",EDGE,"E57"),sQuery(id+"F16.wireOp",EDGE,"E60")])]});var subQ3=makeQuery(id+"F33.imprint","INTERSECT",VERTEX,{"derivedFrom":[subQ2,subQ0]});Q1=makeQuery(id+"F33.imprint","IMPRINT",FACE,{"disambiguationData":[TD([[makeQuery(id+"F33.imprint","IMPRINT",EDGE,{"disambiguationData":[TD([[subQ3,-1.0]])],"derivedFrom":subQ0}),-1.0]])]});}
            var Q2;
            {var subQ0=sQuery(id+"F33.wireOp",EDGE,"E99");var subQ1=sQuery(id+"F16.wireOp",EDGE,"E57");var subQ2=sQuery(id+"F0.wireOp",EDGE,"E3");var subQ3=makeQuery(id+"F17.opExtrude","SWEPT_EDGE",EDGE,{"disambiguationData":[OSD([subQ2,subQ1,sQuery(id+"F16.wireOp",EDGE,"E58")])]});var subQ4=makeQuery(id+"F33.imprint","INTERSECT",VERTEX,{"derivedFrom":[subQ3,subQ0]});Q2=makeQuery(id+"F33.imprint","IMPRINT",FACE,{"disambiguationData":[TD([[makeQuery(id+"F33.imprint","IMPRINT",EDGE,{"disambiguationData":[TD([[subQ4,-1.0]])],"derivedFrom":subQ0}),-1.0]])]});}
            var Q3;
            {var subQ0=sQuery(id+"F33.wireOp",EDGE,"E99");var subQ1=sQuery(id+"F0.wireOp",EDGE,"E3");var subQ2=makeQuery(id+"F17.opExtrude","SWEPT_EDGE",EDGE,{"disambiguationData":[OSD([subQ1,sQuery(id+"F16.wireOp",EDGE,"E69"),sQuery(id+"F16.wireOp",EDGE,"E70")])]});var subQ3=makeQuery(id+"F33.imprint","INTERSECT",VERTEX,{"derivedFrom":[subQ2,subQ0]});Q3=makeQuery(id+"F33.imprint","IMPRINT",FACE,{"disambiguationData":[TD([[makeQuery(id+"F33.imprint","IMPRINT",EDGE,{"disambiguationData":[TD([[subQ3,-1.0]])],"derivedFrom":subQ0}),-1.0]])]});}
            var Q4;
            {var subQ0=sQuery(id+"F33.wireOp",EDGE,"E99");var subQ1=sQuery(id+"F16.wireOp",EDGE,"E69");var subQ2=sQuery(id+"F0.wireOp",EDGE,"E3");var subQ3=makeQuery(id+"F17.opExtrude","SWEPT_EDGE",EDGE,{"disambiguationData":[OSD([subQ2,subQ1,sQuery(id+"F16.wireOp",EDGE,"E72")])]});var subQ4=makeQuery(id+"F33.imprint","INTERSECT",VERTEX,{"derivedFrom":[subQ3,subQ0]});Q4=makeQuery(id+"F33.imprint","IMPRINT",FACE,{"disambiguationData":[TD([[makeQuery(id+"F33.imprint","IMPRINT",EDGE,{"disambiguationData":[TD([[subQ4,-1.0]])],"derivedFrom":subQ0}),-1.0]])]});}
            var Q5;
            {var subQ0=sQuery(id+"F33.wireOp",EDGE,"E99");var subQ1=sQuery(id+"F0.wireOp",EDGE,"E3");var subQ2=makeQuery(id+"F17.opExtrude","SWEPT_EDGE",EDGE,{"disambiguationData":[OSD([subQ1,sQuery(id+"F16.wireOp",EDGE,"E41"),sQuery(id+"F16.wireOp",EDGE,"E47")])]});var subQ3=makeQuery(id+"F33.imprint","INTERSECT",VERTEX,{"derivedFrom":[subQ2,subQ0]});Q5=makeQuery(id+"F33.imprint","IMPRINT",FACE,{"disambiguationData":[TD([[makeQuery(id+"F33.imprint","IMPRINT",EDGE,{"disambiguationData":[TD([[subQ3,-1.0]])],"derivedFrom":subQ0}),-1.0]])]});}
            var Q6;
            {var subQ7=sQuery(id+"F33.wireOp",EDGE,"E101");Q6=makeQuery(id+"F33.imprint","IMPRINT",FACE,{"disambiguationData":[TD([[makeQuery(id+"F33.imprint","IMPRINT",EDGE,{"derivedFrom":subQ7}),1.0]])]});}
            extrude(context, id + "F34", {"entities" : qUnion([Q0, Q1, Q2, Q3, Q4, Q5, Q6]), "operationType" : NewBodyOperationType.ADD, "oppositeDirection" : true, "depth" : 25.4 * mm});
        }
        {
            var Q0;
            Q0=makeQuery(id+"F17.boolean.opBoolean","MERGE",FACE,{"derivedFrom":[makeQuery(id+"F1.opExtrude","SWEPT_FACE",FACE,{"disambiguationData":[OSD([sQuery(id+"F0.wireOp",EDGE,"E2"),sQuery(id+"F0.wireOp",EDGE,"E4")])]}),makeQuery(id+"F17.opExtrude","SWEPT_FACE",FACE,{"disambiguationData":[OSD([sQuery(id+"F16.wireOp",EDGE,"E38")])]}),makeQuery(id+"F17.opExtrude","SWEPT_FACE",FACE,{"disambiguationData":[OSD([sQuery(id+"F16.wireOp",EDGE,"E39")])]})]});
            var sketch = newSketch(context, id + "F35", { "sketchPlane" : qUnion([Q0])});
            skLineSegment(sketch, "E103.bottom", {"start": v(-1371.6, 1543.05) * mm, "end": v(-1066.8, 1543.05) * mm});
            skLineSegment(sketch, "E103.top", {"start": v(-1371.6, 1492.25) * mm, "end": v(-1066.8, 1492.25) * mm});
            skLineSegment(sketch, "E103.left", {"start": v(-1371.6, 1543.05) * mm, "end": v(-1371.6, 1492.25) * mm});
            skLineSegment(sketch, "E103.right", {"start": v(-1066.8, 1543.05) * mm, "end": v(-1066.8, 1492.25) * mm});
            skSolve(sketch);
        }
        {
            var Q0;
            {var subQ0=sQuery(id+"F35.wireOp",EDGE,"E103.left");Q0=makeQuery(id+"F35.imprint","IMPRINT",FACE,{"disambiguationData":[TD([[makeQuery(id+"F35.imprint","IMPRINT",EDGE,{"derivedFrom":subQ0}),1.0]])]});}
            var Q1;
            {var subQ0=sQuery(id+"F35.wireOp",EDGE,"E103.bottom");var subQ1=sQuery(id+"F0.wireOp",EDGE,"E4");var subQ2=sQuery(id+"F0.wireOp",EDGE,"E2");var subQ3=makeQuery(id+"F17.opExtrude","SWEPT_EDGE",EDGE,{"disambiguationData":[OSD([subQ2,subQ1,sQuery(id+"F16.wireOp",EDGE,"E39"),sQuery(id+"F16.wireOp",EDGE,"E51")])]});var subQ4=makeQuery(id+"F35.imprint","INTERSECT",VERTEX,{"derivedFrom":[subQ3,subQ0]});var subQ5=makeQuery(id+"F17.opExtrude","SWEPT_EDGE",EDGE,{"disambiguationData":[OSD([subQ2,subQ1,sQuery(id+"F16.wireOp",EDGE,"E38"),sQuery(id+"F16.wireOp",EDGE,"E53")])]});var subQ6=makeQuery(id+"F35.imprint","INTERSECT",VERTEX,{"derivedFrom":[subQ5,subQ0]});Q1=makeQuery(id+"F35.imprint","IMPRINT",FACE,{"disambiguationData":[TD([[makeQuery(id+"F35.imprint","IMPRINT",EDGE,{"disambiguationData":[TD([[subQ4,1.0],[subQ6,-1.0]])],"derivedFrom":subQ0}),-1.0]])]});}
            var Q2;
            {var subQ0=sQuery(id+"F35.wireOp",EDGE,"E103.right");Q2=makeQuery(id+"F35.imprint","IMPRINT",FACE,{"disambiguationData":[TD([[makeQuery(id+"F35.imprint","IMPRINT",EDGE,{"derivedFrom":subQ0}),-1.0]])]});}
            extrude(context, id + "F36", {"entities" : qUnion([Q0, Q1, Q2]), "operationType" : NewBodyOperationType.ADD, "oppositeDirection" : true, "depth" : 25.4 * mm});
        }
        {
            var Q0;
            Q0=makeQuery(id+"F13.boolean.opBoolean","MERGE",FACE,{"derivedFrom":[makeQuery(id+"F3.boolean.opBoolean","MERGE",FACE,{"derivedFrom":[makeQuery(id+"F1.opExtrude","SWEPT_FACE",FACE,{"disambiguationData":[OSD([sQuery(id+"F0.wireOp",EDGE,"E0.bottom")])]}),makeQuery(id+"F3.opExtrude","SWEPT_FACE",FACE,{"disambiguationData":[OSD([sQuery(id+"F2.wireOp",EDGE,"E8.bottom")])]}),makeQuery(id+"F3.opExtrude","SWEPT_FACE",FACE,{"disambiguationData":[OSD([sQuery(id+"F2.wireOp",EDGE,"E9.bottom")])]}),makeQuery(id+"F3.opExtrude","SWEPT_FACE",FACE,{"disambiguationData":[OSD([sQuery(id+"F2.wireOp",EDGE,"E12.bottom")])]}),makeQuery(id+"F3.opExtrude","SWEPT_FACE",FACE,{"disambiguationData":[OSD([sQuery(id+"F2.wireOp",EDGE,"E13.bottom")])]}),makeQuery(id+"F3.opExtrude","SWEPT_FACE",FACE,{"disambiguationData":[OSD([sQuery(id+"F2.wireOp",EDGE,"E14.bottom")])]}),makeQuery(id+"F3.opExtrude","SWEPT_FACE",FACE,{"disambiguationData":[OSD([sQuery(id+"F2.wireOp",EDGE,"E15.bottom")])]})]}),makeQuery(id+"F13.opExtrude","SWEPT_FACE",FACE,{"disambiguationData":[OSD([sQuery(id+"F12.wireOp",EDGE,"E34.left")])]})]});
            var sketch = newSketch(context, id + "F37", { "sketchPlane" : qUnion([Q0])});
            skLineSegment(sketch, "E104.bottom", {"start": v(3048, 1898.65) * mm, "end": v(3022.6, 1898.65) * mm});
            skLineSegment(sketch, "E104.top", {"start": v(3048, 1847.85) * mm, "end": v(3022.6, 1847.85) * mm});
            skLineSegment(sketch, "E104.left", {"start": v(3048, 1898.65) * mm, "end": v(3048, 1847.85) * mm});
            skLineSegment(sketch, "E104.right", {"start": v(3022.6, 1898.65) * mm, "end": v(3022.6, 1847.85) * mm});
            skSolve(sketch);
        }
        {
            var Q0;
            Q0=makeQuery(id+"F37.imprint","IMPRINT",FACE,{"disambiguationData":[TD([[makeQuery(id+"F37.imprint","IMPRINT",EDGE,{"derivedFrom":sQuery(id+"F37.wireOp",EDGE,"E104.bottom")}),1.0]])]});
            var Q1;
            Q1=makeQuery(id+"F11.boolean.opBoolean","MERGE",FACE,{"derivedFrom":[makeQuery(id+"F3.opExtrude","SWEPT_FACE",FACE,{"disambiguationData":[OSD([sQuery(id+"F2.wireOp",EDGE,"E6.top")])]}),makeQuery(id+"F3.opExtrude","SWEPT_FACE",FACE,{"disambiguationData":[OSD([sQuery(id+"F2.wireOp",EDGE,"E7.top")])]}),makeQuery(id+"F7.boolean.opBoolean","MERGE",FACE,{"derivedFrom":[makeQuery(id+"F3.opExtrude","SWEPT_FACE",FACE,{"disambiguationData":[OSD([sQuery(id+"F2.wireOp",EDGE,"E10.top")])]}),makeQuery(id+"F3.opExtrude","SWEPT_FACE",FACE,{"disambiguationData":[OSD([sQuery(id+"F2.wireOp",EDGE,"E11.top")])]}),makeQuery(id+"F5.opExtrude","SWEPT_FACE",FACE,{"disambiguationData":[OSD([sQuery(id+"F4.wireOp",EDGE,"E25.top")])]}),makeQuery(id+"F5.opExtrude","SWEPT_FACE",FACE,{"disambiguationData":[OSD([sQuery(id+"F4.wireOp",EDGE,"E26.top")])]}),makeQuery(id+"F7.opExtrude","SWEPT_FACE",FACE,{"disambiguationData":[OSD([sQuery(id+"F6.wireOp",EDGE,"E29.right")])]}),makeQuery(id+"F7.opExtrude","SWEPT_FACE",FACE,{"disambiguationData":[OSD([sQuery(id+"F6.wireOp",EDGE,"E30.right")])]})]}),makeQuery(id+"F11.opExtrude","SWEPT_FACE",FACE,{"disambiguationData":[OSD([sQuery(id+"F10.wireOp",EDGE,"E33.left")])]})]});
            extrude(context, id + "F38", {"entities" : qUnion([Q0]), "operationType" : NewBodyOperationType.ADD, "endBound" : BoundingType.UP_TO_SURFACE, "oppositeDirection" : true, "endBoundEntityFace" : qUnion([Q1]), "depth" : 25.4 * mm});
        }
        {
            var Q0;
            {var subQ5=sQuery(id+"F25.wireOp",EDGE,"E81");var subQ10=sQuery(id+"F0.wireOp",EDGE,"E0.bottom");var subQ11=sQuery(id+"F29.wireOp",EDGE,"E92");var subQ12=makeQuery(id+"F30.opExtrude","SWEPT_FACE",FACE,{"disambiguationData":[OSD([subQ11])]});var subQ18=sQuery(id+"F2.wireOp",EDGE,"E22");var subQ19=sQuery(id+"F2.wireOp",EDGE,"E19");var subQ22=sQuery(id+"F2.wireOp",EDGE,"E17.left");var subQ42=sQuery(id+"F2.wireOp",EDGE,"E6.left");var subQ43=sQuery(id+"F2.wireOp",EDGE,"E6.top");var subQ49=makeQuery(id+"F3.opExtrude","SWEPT_FACE",FACE,{"disambiguationData":[OSD([subQ43])]});var subQ66=sQuery(id+"F2.wireOp",EDGE,"E8.top");var subQ69=sQuery(id+"F2.wireOp",EDGE,"E16.left");var subQ80=sQuery(id+"F2.wireOp",EDGE,"E9.left");var subQ84=makeQuery(id+"F3.opExtrude","SWEPT_FACE",FACE,{"disambiguationData":[OSD([subQ18])]});var subQ92=sQuery(id+"F27.wireOp",EDGE,"E85");var subQ109=sQuery(id+"F29.wireOp",EDGE,"E87");var subQ111=makeQuery(id+"F15.boolean.opBoolean","MERGE",FACE,{"derivedFrom":[makeQuery(id+"F3.opExtrude","SWEPT_FACE",FACE,{"disambiguationData":[OSD([subQ42])]}),makeQuery(id+"F3.opExtrude","SWEPT_FACE",FACE,{"disambiguationData":[OSD([subQ80])]}),makeQuery(id+"F3.opExtrude","SWEPT_FACE",FACE,{"disambiguationData":[OSD([subQ69])]}),makeQuery(id+"F3.opExtrude","SWEPT_FACE",FACE,{"disambiguationData":[OSD([subQ22])]}),makeQuery(id+"F3.opExtrude","SWEPT_FACE",FACE,{"disambiguationData":[OSD([subQ19])]}),makeQuery(id+"F15.opExtrude","SWEPT_FACE",FACE,{"disambiguationData":[OSD([sQuery(id+"F14.wireOp",EDGE,"E35.left")])]})]});var subQ112=makeQuery(id+"F19.boolean.opBoolean","SPLIT",FACE,{"disambiguationData":[TD([subQ49])],"derivedFrom":subQ111});Q0=makeQuery(id+"F32.boolean.opBoolean","SPLIT",FACE,{"disambiguationData":[TD([makeQuery(id+"F1.opExtrude","SWEPT_FACE",FACE,{"disambiguationData":[OSD([subQ10])]})])],"derivedFrom":makeQuery(id+"F30.boolean.opBoolean","MERGE",FACE,{"derivedFrom":[makeQuery(id+"F28.boolean.opBoolean","MERGE",FACE,{"derivedFrom":[makeQuery(id+"F19.boolean.opBoolean","SPLIT",FACE,{"disambiguationData":[TD([makeQuery(id+"F3.opExtrude","SWEPT_FACE",FACE,{"disambiguationData":[OSD([subQ66])]})])],"derivedFrom":subQ111}),makeQuery(id+"F26.boolean.opBoolean","MERGE",FACE,{"derivedFrom":[makeQuery(id+"F23.boolean.opBoolean","SPLIT",FACE,{"disambiguationData":[TD([subQ84])],"derivedFrom":subQ112}),makeQuery(id+"F23.boolean.opBoolean","SPLIT",FACE,{"disambiguationData":[TD([subQ49])],"derivedFrom":subQ112}),makeQuery(id+"F26.opExtrude","SWEPT_FACE",FACE,{"disambiguationData":[OSD([subQ5])]})]}),makeQuery(id+"F28.opExtrude","SWEPT_FACE",FACE,{"disambiguationData":[OSD([subQ92])]})]}),makeQuery(id+"F30.opExtrude","SWEPT_FACE",FACE,{"disambiguationData":[OSD([subQ109])]}),subQ12]})});}
            var sketch = newSketch(context, id + "F39", { "sketchPlane" : qUnion([Q0])});
            skLineSegment(sketch, "E105", {"start": v(-2361.26, 1561.43) * mm, "end": v(-2361.26, 1949.45) * mm});
            skLineSegment(sketch, "E106", {"start": v(-2361.26, 1561.43) * mm, "end": v(-2413, 1551.82) * mm});
            skLineSegment(sketch, "E107", {"start": v(-2413, 1551.82) * mm, "end": v(-2413, 1942.75) * mm});
            skLineSegment(sketch, "E108", {"start": v(-2413, 1942.75) * mm, "end": v(-2404.65, 1941.2) * mm});
            skLineSegment(sketch, "E109", {"start": v(-2404.65, 1941.2) * mm, "end": v(-2361.26, 1949.45) * mm});
            skLineSegment(sketch, "E110", {"start": v(-2361.26, 1561.43) * mm, "end": v(-2305, 1561.43) * mm});
            skLineSegment(sketch, "E111", {"start": v(-2305, 1561.43) * mm, "end": v(-2305, 1949.45) * mm});
            skLineSegment(sketch, "E112", {"start": v(-2305, 1949.45) * mm, "end": v(-2361.26, 1949.45) * mm});
            skSolve(sketch);
        }
        {
            var Q0;
            Q0=makeQuery(id+"F39.imprint","IMPRINT",FACE,{"disambiguationData":[TD([[makeQuery(id+"F39.imprint","IMPRINT",EDGE,{"derivedFrom":sQuery(id+"F39.wireOp",EDGE,"E105")}),1.0]])]});
            var Q1;
            Q1=makeQuery(id+"F39.imprint","IMPRINT",FACE,{"disambiguationData":[TD([[makeQuery(id+"F39.imprint","IMPRINT",EDGE,{"derivedFrom":sQuery(id+"F39.wireOp",EDGE,"E105")}),-1.0]])]});
            extrude(context, id + "F40", {"entities" : qUnion([Q0, Q1]), "operationType" : NewBodyOperationType.REMOVE, "oppositeDirection" : true, "depth" : 25.4 * mm});
        }
    });
